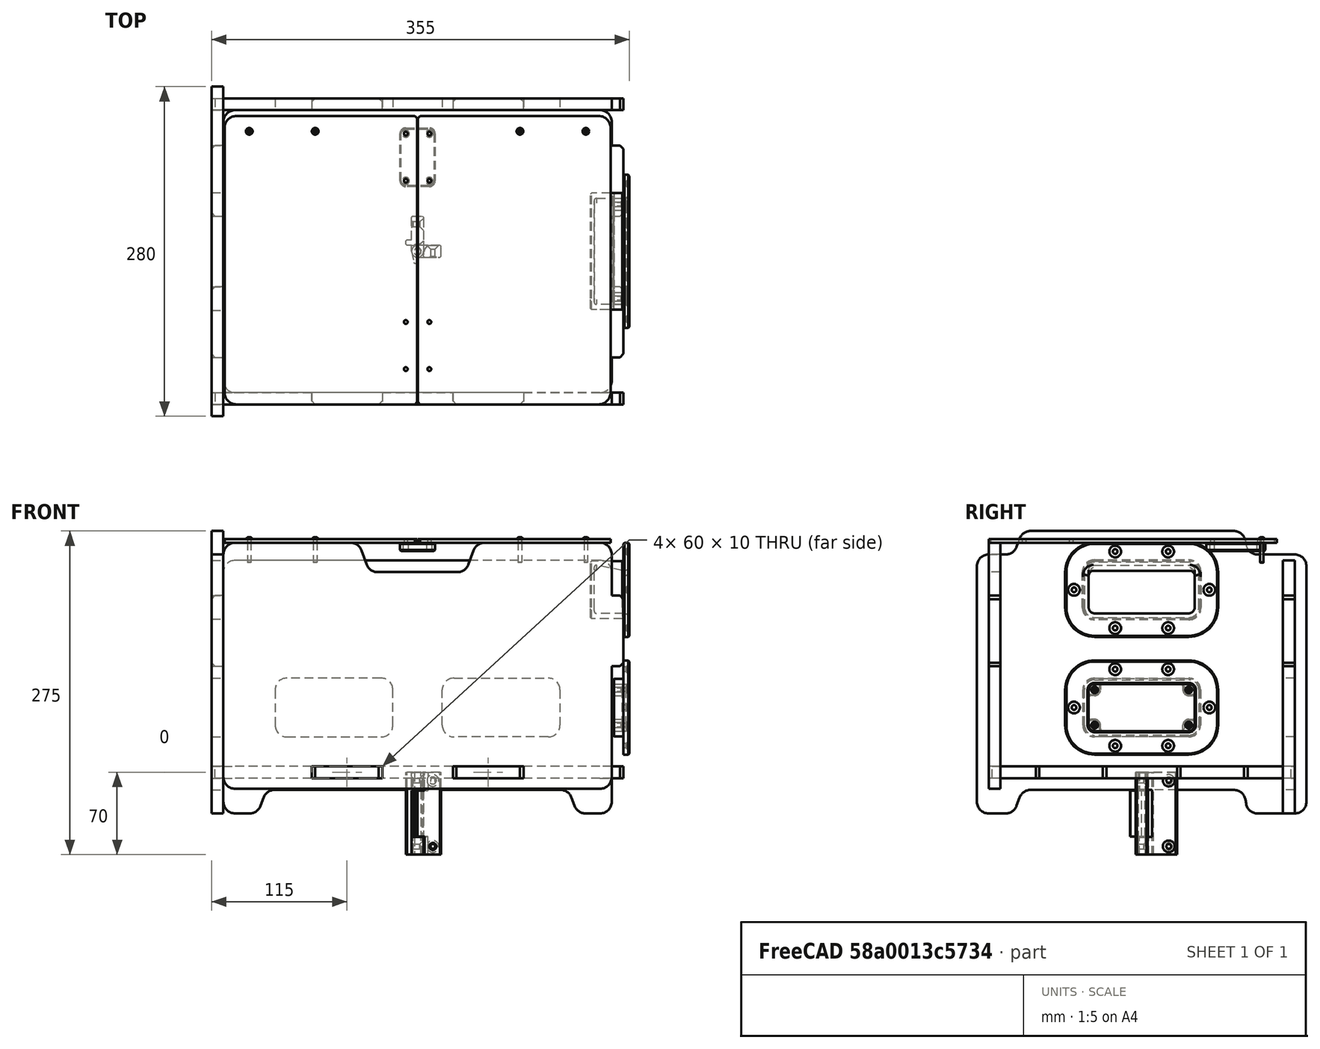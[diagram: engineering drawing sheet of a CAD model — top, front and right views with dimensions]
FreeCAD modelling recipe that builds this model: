
FCSTD DOCUMENT  (FreeCAD 2024.113R14555 (Git shallow))
Label: ModularCrate
License: Creative Commons Attribution-NoDerivatives
LicenseURL: http://creativecommons.org/licenses/by-nd/4.0/
objects: Sketcher::SketchObject×37, PartDesign::Pocket×22, PartDesign::Chamfer×19, PartDesign::Pad×16, PartDesign::Fillet×13, PartDesign::Body×12, App::Link×8, Part::FeaturePython×8, Part::SubShapeBinder×7, TechDraw::DrawSVGTemplate×7, TechDraw::DrawProjGroupItem×7, TechDraw::DrawProjGroup×7, TechDraw::DrawPage×7, App::DocumentObjectGroup×7, PartDesign::Mirrored×6, PartDesign::Plane×5, App::Part×3, PartDesign::FeatureBase×3, PartDesign::SubShapeBinder×2, TechDraw::DrawViewDimension×2, +2 more types
note: 348 computed .brp shape members not serialized (recipe doc carries the construction recipe); baked Part::Feature solids carry a one-line shape summary decoded from their .brp

FEATURE [Sketcher::SketchObject] Sketch007
  ArcFitTolerance = 1e-06
  AttachmentSupport = -> [XY_Plane003]
  ExternalBSplineMaxDegree = 5
  ExternalBSplineTolerance = 0.0001
  FullyConstrained = true
  InternalTolerance = 1e-06
  InvalidShape = false
  MakeInternals = true
  MapMode = 5
  Support = -> [XY_Plane003]
  TreeRank = 69
  ValidateShape = true
  sketch-geometry (10):
    g0: Circle CenterX=-9.7632e-12 CenterY=-2.88622e-11 CenterZ=0 NormalX=0 NormalY=0 NormalZ=1 AngleXU=0 Radius=2.75
    g1: ArcOfCircle CenterX=-9.7632e-12 CenterY=-2.88622e-11 CenterZ=0 NormalX=0 NormalY=0 NormalZ=1 AngleXU=0 Radius=5 StartAngle=3.14159 EndAngle=6.28319
    g2: LineSegment StartX=-5 StartY=-3.9183e-11 StartZ=0 EndX=-5 EndY=5 EndZ=0
    g3: LineSegment StartX=-5 StartY=5 StartZ=0 EndX=-10 EndY=5 EndZ=0
    g4: LineSegment StartX=-10 StartY=5 StartZ=0 EndX=-10 EndY=10 EndZ=0
    g5: LineSegment StartX=-10 StartY=10 StartZ=0 EndX=-5 EndY=10 EndZ=0
    g6: LineSegment StartX=-5 StartY=10 StartZ=0 EndX=-5 EndY=30 EndZ=0
    g7: LineSegment StartX=-5 StartY=30 StartZ=0 EndX=5 EndY=30 EndZ=0
    g8: LineSegment StartX=5 StartY=30 StartZ=0 EndX=5 EndY=7.47242e-11 EndZ=0
    g9: Circle [constr] CenterX=-9.7632e-12 CenterY=-2.88622e-11 CenterZ=0 NormalX=0 NormalY=0 NormalZ=1 AngleXU=0 Radius=5
  constraints (28):
    c: Coincident(g0,g-1)
    c: Coincident(g1,g0)
    c: PointOnObject(g1,g-1)
    c: PointOnObject(g2,g-1)
    c: Vertical(g2)
    c: Coincident(g1,g2)
    c: Coincident(g3,g2)
    c: Horizontal(g3)
    c: Coincident(g4,g3)
    c: Coincident(g5,g4)
    c: Horizontal(g5)
    c: Vertical(g4)
    c: DistanceY(g4,g4) = 5
    c: Diameter(g0) = 5.5
    c: Diameter(g1) = 10
    c: DistanceX(g5,g5) = 5
    c: Vertical(g6)
    c: Coincident(g7,g6)
    c: Horizontal(g7)
    c: Coincident(g8,g1)
    c: Vertical(g8)
    c: Coincident(g8,g7)
    c: Coincident(g5,g6)
    c: PointOnObject(g2,g6)
    c: DistanceY(g6,g6) = 20
    c: Coincident(g9,g0)
    c: PointOnObject(g1,g9)
    c: Tangent(g3,g9)
FEATURE [PartDesign::Pad] Pad004
  AddSubType = 0
  AlongSketchNormal = false
  AutoTaperInnerAngle = true
  CheckUpToFaceLimits = true
  ClaimChildren = false
  Direction = (0,0,1)
  Fit = 0
  FitJoin = 0
  InnerFit = 0
  InnerFitJoin = 0
  InvalidShape = false
  Length = 70
  Length2 = 100
  Linearize = true
  Midplane = true
  NewSolid = false
  Profile = -> Sketch007
  Refine = true
  Suppress = false
  TaperInnerAngle = 0
  TaperInnerAngleRev = 0
  TreeRank = 70
  Type = 0
  ValidateShape = true
  _ProfileBasedVersion = 1
FEATURE [Sketcher::SketchObject] Sketch008
  ArcFitTolerance = 1e-06
  AttachmentSupport = -> [XY_Plane003]
  ExternalBSplineMaxDegree = 5
  ExternalBSplineTolerance = 0.0001
  FullyConstrained = true
  InternalTolerance = 1e-06
  InvalidShape = false
  MakeInternals = true
  MapMode = 5
  Support = -> [XY_Plane003]
  TreeRank = 71
  ValidateShape = true
  sketch-geometry (5):
    g0: LineSegment StartX=-5 StartY=-5 StartZ=0 EndX=-5 EndY=5 EndZ=0
    g1: LineSegment StartX=-5 StartY=5 StartZ=0 EndX=5 EndY=5 EndZ=0
    g2: LineSegment StartX=5 StartY=5 StartZ=0 EndX=5 EndY=-5 EndZ=0
    g3: LineSegment StartX=5 StartY=-5 StartZ=0 EndX=-5 EndY=-5 EndZ=0
    g4: GeomPoint [constr] X=0 Y=0 Z=0
  constraints (12):
    c: Coincident(g0,g1)
    c: Coincident(g1,g2)
    c: Coincident(g2,g3)
    c: Coincident(g3,g0)
    c: Horizontal(g1)
    c: Horizontal(g3)
    c: Vertical(g0)
    c: Vertical(g2)
    c: Symmetric(g1,g0,g4)
    c: Coincident(g4,g-1)
    c: DistanceY(g2,g2) = 10
    c: Equal(g3,g2)
FEATURE [PartDesign::Pocket] Pocket003
  AddSubType = 1
  AutoTaperInnerAngle = true
  BaseFeature = -> Pad004
  CheckUpToFaceLimits = true
  ClaimChildren = false
  Direction = (1,1,1)
  Fit = 0
  FitJoin = 0
  InnerFit = 0
  InnerFitJoin = 0
  InvalidShape = false
  Length = 40
  Length2 = 100
  Linearize = true
  Midplane = true
  NewSolid = false
  Profile = -> Sketch008
  Refine = true
  Suppress = false
  TaperInnerAngle = 0
  TaperInnerAngleRev = 0
  TreeRank = 72
  Type = 0
  ValidateShape = true
  _ProfileBasedVersion = 1
  _Version = 1
FEATURE [Sketcher::SketchObject] Sketch009
  ArcFitTolerance = 1e-06
  AttachmentSupport = -> [XY_Plane003]
  ExternalBSplineMaxDegree = 5
  ExternalBSplineTolerance = 0.0001
  FullyConstrained = true
  InternalTolerance = 1e-06
  InvalidShape = false
  MakeInternals = true
  MapMode = 5
  Support = -> [XY_Plane003]
  TreeRank = 73
  ValidateShape = true
  sketch-geometry (1):
    g0: Circle CenterX=0 CenterY=0 CenterZ=0 NormalX=0 NormalY=0 NormalZ=1 AngleXU=0 Radius=6
  constraints (2):
    c: Coincident(g0,g-1)
    c: Diameter(g0) = 12
FEATURE [PartDesign::Pocket] Pocket004
  AddSubType = 1
  AutoTaperInnerAngle = true
  BaseFeature = -> Pocket003
  CheckUpToFaceLimits = true
  ClaimChildren = false
  Direction = (1,1,1)
  Fit = 0
  FitJoin = 0
  InnerFit = 0
  InnerFitJoin = 0
  InvalidShape = false
  Length = 40
  Length2 = 100
  Linearize = true
  Midplane = true
  NewSolid = false
  Profile = -> Sketch009
  Refine = true
  Suppress = false
  TaperInnerAngle = 0
  TaperInnerAngleRev = 0
  TreeRank = 74
  Type = 0
  ValidateShape = true
  _ProfileBasedVersion = 1
  _Version = 1
FEATURE [PartDesign::Chamfer] Chamfer007
  AddSubType = 0
  Angle = 45
  Base = -> Pocket004 [Edge33]
  BaseFeature = -> Pocket004
  ChamferType = 0
  FlipDirection = false
  InvalidShape = false
  NewSolid = false
  Refine = true
  Size = 0.4
  Size2 = 1
  SupportTransform = false
  Suppress = false
  TreeRank = 75
  UseAllEdges = false
  ValidateShape = true
FEATURE [PartDesign::Chamfer] Chamfer008
  AddSubType = 0
  Angle = 45
  Base = -> Chamfer007 [Edge16,Edge27,Edge44,Edge34]
  BaseFeature = -> Chamfer007
  ChamferType = 0
  FlipDirection = false
  InvalidShape = false
  NewSolid = false
  Refine = true
  Size = 0.4
  Size2 = 1
  SupportTransform = false
  Suppress = false
  TreeRank = 76
  UseAllEdges = false
  ValidateShape = true
FEATURE [PartDesign::Chamfer] Chamfer009
  AddSubType = 0
  Angle = 45
  Base = -> Chamfer008 [Edge17,Edge47,Edge33,Edge54]
  BaseFeature = -> Chamfer008
  ChamferType = 0
  FlipDirection = false
  InvalidShape = false
  NewSolid = false
  Refine = true
  Size = 1
  Size2 = 1
  SupportTransform = false
  Suppress = false
  TreeRank = 77
  UseAllEdges = false
  ValidateShape = true
FEATURE [Sketcher::SketchObject] Sketch010
  ArcFitTolerance = 1e-06
  AttachmentSupport = -> [XY_Plane004]
  ExternalBSplineMaxDegree = 5
  ExternalBSplineTolerance = 0.0001
  FullyConstrained = true
  InternalTolerance = 1e-06
  InvalidShape = false
  MakeInternals = true
  MapMode = 5
  Support = -> [XY_Plane004]
  TreeRank = 88
  ValidateShape = true
  sketch-geometry (8):
    g0: Circle CenterX=-1.7078e-12 CenterY=-5.9561e-12 CenterZ=0 NormalX=0 NormalY=0 NormalZ=1 AngleXU=0 Radius=2.75
    g1: ArcOfCircle CenterX=-1.7078e-12 CenterY=-5.9561e-12 CenterZ=0 NormalX=0 NormalY=0 NormalZ=1 AngleXU=0 Radius=5 StartAngle=8.015e-13 EndAngle=1.5708
    g2: LineSegment StartX=-8.718e-13 StartY=5 StartZ=0 EndX=-10 EndY=3 EndZ=0
    g3: LineSegment StartX=-10 StartY=3 StartZ=0 EndX=-10 EndY=0 EndZ=0
    g4: LineSegment StartX=-10 StartY=0 StartZ=0 EndX=-5 EndY=-1.52707e-11 EndZ=0
    g5: LineSegment StartX=-5 StartY=-1.52707e-11 StartZ=0 EndX=-5 EndY=-20 EndZ=0
    g6: LineSegment StartX=-5 StartY=-20 StartZ=0 EndX=5 EndY=-20 EndZ=0
    g7: LineSegment StartX=5 StartY=-20 StartZ=0 EndX=5 EndY=-7.851e-13 EndZ=0
  constraints (22):
    c: Coincident(g0,g-1)
    c: Diameter(g0) = 5.5
    c: Coincident(g1,g0)
    c: PointOnObject(g1,g-2)
    c: PointOnObject(g1,g-1)
    c: Diameter(g1) = 10
    c: Coincident(g2,g1)
    c: Coincident(g3,g2)
    c: PointOnObject(g3,g-1)
    c: Vertical(g3)
    c: Coincident(g4,g3)
    c: Coincident(g5,g4)
    c: Vertical(g5)
    c: Coincident(g6,g5)
    c: Horizontal(g6)
    c: Coincident(g7,g1)
    c: Vertical(g7)
    c: Coincident(g6,g7)
    c: Symmetric(g4,g1,g0)
    c: DistanceX(g4,g4) = 5
    c: DistanceY(g3,g3) = 3
    c: DistanceY(g5,g5) = 20
FEATURE [PartDesign::Pad] Pad005
  AddSubType = 0
  AlongSketchNormal = false
  AutoTaperInnerAngle = true
  CheckUpToFaceLimits = true
  ClaimChildren = false
  Direction = (0,0,1)
  Fit = 0
  FitJoin = 0
  InnerFit = 0
  InnerFitJoin = 0
  InvalidShape = false
  Length = 70
  Length2 = 100
  Linearize = true
  Midplane = true
  NewSolid = false
  Profile = -> Sketch010
  Refine = true
  Suppress = false
  TaperInnerAngle = 0
  TaperInnerAngleRev = 0
  TreeRank = 89
  Type = 0
  ValidateShape = true
  _ProfileBasedVersion = 1
FEATURE [Sketcher::SketchObject] Sketch011
  ArcFitTolerance = 1e-06
  AttachmentOffset = pos=(0,0,19.5) rot=(0,0,1;0rad)
  AttachmentSupport = -> [XY_Plane004]
  ExternalBSplineMaxDegree = 5
  ExternalBSplineTolerance = 0.0001
  FullyConstrained = true
  InternalTolerance = 1e-06
  InvalidShape = false
  MakeInternals = true
  MapMode = 5
  Placement = pos=(0,0,19.5) rot=(0,0,1;0rad)
  Support = -> [XY_Plane004]
  TreeRank = 90
  ValidateShape = true
  sketch-geometry (5):
    g0: LineSegment StartX=-15 StartY=5 StartZ=0 EndX=-15 EndY=-5 EndZ=0
    g1: LineSegment StartX=-15 StartY=-5 StartZ=0 EndX=5 EndY=-5 EndZ=0
    g2: LineSegment StartX=5 StartY=-5 StartZ=0 EndX=5 EndY=5 EndZ=0
    g3: LineSegment StartX=5 StartY=5 StartZ=0 EndX=-15 EndY=5 EndZ=0
    g4: GeomPoint [constr] X=-5 Y=1.1738e-12 Z=0
  constraints (13):
    c: Coincident(g0,g1)
    c: Coincident(g1,g2)
    c: Coincident(g2,g3)
    c: Coincident(g3,g0)
    c: Horizontal(g1)
    c: Horizontal(g3)
    c: Vertical(g0)
    c: Vertical(g2)
    c: Symmetric(g1,g0,g4)
    c: PointOnObject(g4,g-1)
    c: DistanceY(g2,g2) = 10
    c: DistanceX(g-1,g2) = 5
    c: DistanceX(g3,g3) = 20
FEATURE [PartDesign::Pocket] Pocket005
  AddSubType = 1
  AutoTaperInnerAngle = true
  BaseFeature = -> Pad005
  CheckUpToFaceLimits = true
  ClaimChildren = false
  Direction = (1,1,1)
  Fit = 0
  FitJoin = 0
  InnerFit = 0
  InnerFitJoin = 0
  InvalidShape = false
  Length = 5
  Length2 = 100
  Linearize = true
  NewSolid = false
  Profile = -> Sketch011
  Refine = true
  Reversed = true
  Suppress = false
  TaperInnerAngle = 0
  TaperInnerAngleRev = 0
  TreeRank = 91
  Type = 1
  ValidateShape = true
  _ProfileBasedVersion = 1
  _Version = 1
FEATURE [PartDesign::Mirrored] Mirrored
  AddSubType = 0
  BaseFeature = -> Pocket005
  CopyShape = false
  InvalidShape = false
  MirrorPlane = -> XY_Plane004
  NewSolid = false
  OriginalSubs = -> [Pocket005]
  Originals = -> [Pocket005]
  ParallelTransform = true
  Refine = true
  SubTransform = true
  Suppress = false
  TreeRank = 92
  ValidateShape = true
  _Version = 3
FEATURE [PartDesign::Chamfer] Chamfer010
  AddSubType = 0
  Angle = 45
  Base = -> Mirrored [Edge12,Edge32]
  BaseFeature = -> Mirrored
  ChamferType = 0
  FlipDirection = false
  InvalidShape = false
  NewSolid = false
  Refine = true
  Size = 0.4
  Size2 = 1
  SupportTransform = false
  Suppress = false
  TreeRank = 93
  UseAllEdges = false
  ValidateShape = true
FEATURE [Sketcher::SketchObject] Sketch012
  ArcFitTolerance = 1e-06
  AttachmentSupport = -> [Chamfer010]
  ExternalBSplineMaxDegree = 5
  ExternalBSplineTolerance = 0.0001
  FullyConstrained = true
  InternalTolerance = 1e-06
  InvalidShape = false
  MakeInternals = true
  MapMode = 5
  Placement = pos=(0,0,19.5) rot=(0,0,1;0rad)
  Support = -> [Chamfer010]
  TreeRank = 94
  ValidateShape = true
  sketch-geometry (1):
    g0: Circle CenterX=0 CenterY=0 CenterZ=0 NormalX=0 NormalY=0 NormalZ=1 AngleXU=0 Radius=5.5
  constraints (2):
    c: Coincident(g0,g-1)
    c: Diameter(g0) = 11
FEATURE [PartDesign::Pocket] Pocket006
  AddSubType = 1
  AutoTaperInnerAngle = true
  BaseFeature = -> Chamfer010
  CheckUpToFaceLimits = true
  ClaimChildren = false
  Direction = (1,1,1)
  Fit = 0
  FitJoin = 0
  InnerFit = 0
  InnerFitJoin = 0
  InvalidShape = false
  Length = 5
  Length2 = 100
  Linearize = true
  NewSolid = false
  Profile = -> Sketch012
  Refine = true
  Reversed = true
  Suppress = false
  TaperInnerAngle = 0
  TaperInnerAngleRev = 0
  TreeRank = 95
  Type = 1
  ValidateShape = true
  _ProfileBasedVersion = 1
  _Version = 1
FEATURE [PartDesign::Mirrored] Mirrored001
  AddSubType = 0
  BaseFeature = -> Pocket006
  CopyShape = false
  InvalidShape = false
  MirrorPlane = -> XY_Plane004
  NewSolid = false
  OriginalSubs = -> [Pocket006]
  Originals = -> [Pocket006]
  ParallelTransform = true
  Refine = true
  SubTransform = true
  Suppress = false
  TreeRank = 96
  ValidateShape = true
  _Version = 3
FEATURE [PartDesign::Chamfer] Chamfer011
  AddSubType = 0
  Angle = 45
  Base = -> Mirrored001 [Edge52,Edge50,Edge42,Edge40]
  BaseFeature = -> Mirrored001
  ChamferType = 0
  FlipDirection = false
  InvalidShape = false
  NewSolid = false
  Refine = true
  Size = 0.4
  Size2 = 1
  SupportTransform = false
  Suppress = false
  TreeRank = 97
  UseAllEdges = false
  ValidateShape = true
FEATURE [PartDesign::Chamfer] Chamfer012
  AddSubType = 0
  Angle = 45
  Base = -> Chamfer011 [Edge16,Edge34,Edge39,Edge25,Edge21,Edge43]
  BaseFeature = -> Chamfer011
  ChamferType = 0
  FlipDirection = false
  InvalidShape = false
  NewSolid = false
  Refine = true
  Size = 1
  Size2 = 1
  SupportTransform = false
  Suppress = false
  TreeRank = 98
  UseAllEdges = false
  ValidateShape = true
FEATURE [Sketcher::SketchObject] Sketch013
  ArcFitTolerance = 1e-06
  AttachmentSupport = -> [YZ_Plane004]
  ExternalBSplineMaxDegree = 5
  ExternalBSplineTolerance = 0.0001
  ExternalGeometry = -> [Chamfer012]
  FullyConstrained = true
  InternalTolerance = 1e-06
  InvalidShape = false
  MakeInternals = true
  MapMode = 5
  Placement = pos=(0,0,0) rot=(0.57735,0.57735,0.57735;2.0944rad)
  Support = -> [YZ_Plane004]
  TreeRank = 99
  ValidateShape = true
  sketch-geometry (2):
    g0: Circle CenterX=-13 CenterY=28 CenterZ=0 NormalX=0 NormalY=0 NormalZ=1 AngleXU=0 Radius=2
    g1: Circle CenterX=-13 CenterY=-28 CenterZ=0 NormalX=0 NormalY=0 NormalZ=1 AngleXU=0 Radius=2
  constraints (5):
    c: Diameter(g0) = 4
    c: DistanceX(g-3,g0) = 7
    c: DistanceY(g0,g-3) = 7
    c: Equal(g1,g0)
    c: Symmetric(g1,g0,g-1)
FEATURE [PartDesign::Pocket] Pocket007
  AddSubType = 1
  AutoTaperInnerAngle = true
  BaseFeature = -> Chamfer012
  CheckUpToFaceLimits = true
  ClaimChildren = false
  Direction = (1,1,1)
  Fit = 0
  FitJoin = 0
  InnerFit = 0
  InnerFitJoin = 0
  InvalidShape = false
  Length = 5
  Length2 = 100
  Linearize = true
  Midplane = true
  NewSolid = false
  Profile = -> Sketch013
  Refine = true
  Suppress = false
  TaperInnerAngle = 0
  TaperInnerAngleRev = 0
  TreeRank = 100
  Type = 1
  ValidateShape = true
  _ProfileBasedVersion = 1
  _Version = 1
FEATURE [PartDesign::Chamfer] Chamfer013
  AddSubType = 0
  Angle = 45
  Base = -> Pocket007 [Edge34,Edge33]
  BaseFeature = -> Pocket007
  ChamferType = 0
  FlipDirection = false
  InvalidShape = false
  NewSolid = false
  Refine = true
  Size = 1
  Size2 = 1
  SupportTransform = false
  Suppress = false
  TreeRank = 101
  UseAllEdges = false
  ValidateShape = true
FEATURE [Sketcher::SketchObject] Sketch014
  ArcFitTolerance = 1e-06
  AttachmentSupport = -> [YZ_Plane003]
  ExternalBSplineMaxDegree = 5
  ExternalBSplineTolerance = 0.0001
  ExternalGeometry = -> [Chamfer009]
  FullyConstrained = true
  InternalTolerance = 1e-06
  InvalidShape = false
  MakeInternals = true
  MapMode = 5
  Placement = pos=(0,0,0) rot=(0.57735,0.57735,0.57735;2.0944rad)
  Support = -> [YZ_Plane003]
  TreeRank = 102
  ValidateShape = true
  sketch-geometry (2):
    g0: Circle CenterX=23 CenterY=28 CenterZ=0 NormalX=0 NormalY=0 NormalZ=1 AngleXU=0 Radius=2
    g1: Circle CenterX=23 CenterY=-28 CenterZ=0 NormalX=0 NormalY=0 NormalZ=1 AngleXU=0 Radius=2
  constraints (5):
    c: DistanceX(g0,g-3) = 7
    c: DistanceY(g0,g-3) = 7
    c: Symmetric(g1,g0,g-1)
    c: Equal(g1,g0)
    c: Diameter(g1) = 4
FEATURE [PartDesign::Pocket] Pocket008
  AddSubType = 1
  AutoTaperInnerAngle = true
  BaseFeature = -> Chamfer009
  CheckUpToFaceLimits = true
  ClaimChildren = false
  Direction = (1,1,1)
  Fit = 0
  FitJoin = 0
  InnerFit = 0
  InnerFitJoin = 0
  InvalidShape = false
  Length = 5
  Length2 = 100
  Linearize = true
  Midplane = true
  NewSolid = false
  Profile = -> Sketch014
  Refine = true
  Suppress = false
  TaperInnerAngle = 0
  TaperInnerAngleRev = 0
  TreeRank = 103
  Type = 1
  ValidateShape = true
  _ProfileBasedVersion = 1
  _Version = 1
FEATURE [PartDesign::Chamfer] Chamfer014
  AddSubType = 0
  Angle = 45
  Base = -> Pocket008 [Edge64,Edge63]
  BaseFeature = -> Pocket008
  ChamferType = 0
  FlipDirection = false
  InvalidShape = false
  NewSolid = false
  Refine = true
  Size = 1
  Size2 = 1
  SupportTransform = false
  Suppress = false
  TreeRank = 104
  UseAllEdges = false
  ValidateShape = true
FEATURE [PartDesign::Chamfer] Chamfer019
  AddSubType = 0
  Angle = 45
  Base = -> Chamfer014 [Edge45,Edge38]
  BaseFeature = -> Chamfer014
  ChamferType = 0
  FlipDirection = false
  InvalidShape = false
  NewSolid = false
  Refine = true
  Size = 3
  Size2 = 1
  SupportTransform = false
  Suppress = false
  TreeRank = 128
  UseAllEdges = false
  ValidateShape = true
FEATURE [PartDesign::Chamfer] Chamfer020
  AddSubType = 0
  Angle = 45
  Base = -> Chamfer013 [Edge76,Edge87]
  BaseFeature = -> Chamfer013
  ChamferType = 0
  FlipDirection = false
  InvalidShape = false
  NewSolid = false
  Refine = true
  Size = 3
  Size2 = 1
  SupportTransform = false
  Suppress = false
  TreeRank = 129
  UseAllEdges = false
  ValidateShape = true
FEATURE [Sketcher::SketchObject] Sketch017
  ArcFitTolerance = 1e-06
  AttachmentSupport = -> [Chamfer020]
  ExternalBSplineMaxDegree = 5
  ExternalBSplineTolerance = 0.0001
  ExternalGeometry = -> [Chamfer020]
  FullyConstrained = true
  InternalTolerance = 1e-06
  InvalidShape = false
  MakeInternals = true
  MapMode = 5
  Placement = pos=(0,0,35) rot=(0,0,1;0rad)
  Support = -> [Chamfer020]
  TreeRank = 130
  ValidateShape = true
  sketch-geometry (3):
    g0: LineSegment StartX=5 StartY=-5 StartZ=0 EndX=1 EndY=-5 EndZ=0
    g1: LineSegment StartX=1 StartY=-5 StartZ=0 EndX=5 EndY=-9 EndZ=0
    g2: LineSegment StartX=5 StartY=-9 StartZ=0 EndX=5 EndY=-5 EndZ=0
  constraints (8):
    c: Coincident(g0,g-3)
    c: Horizontal(g0)
    c: Coincident(g2,g1)
    c: Coincident(g2,g0)
    c: Coincident(g0,g1)
    c: Vertical(g2)
    c: Equal(g2,g0)
    c: DistanceY(g2,g2) = 4
FEATURE [PartDesign::Pocket] Pocket010
  AddSubType = 1
  AutoTaperInnerAngle = true
  BaseFeature = -> Chamfer020
  CheckUpToFaceLimits = true
  ClaimChildren = false
  Direction = (1,1,1)
  Fit = 0
  FitJoin = 0
  InnerFit = 0
  InnerFitJoin = 0
  InvalidShape = false
  Length = 15.5
  Length2 = 100
  Linearize = true
  NewSolid = false
  Profile = -> Sketch017
  Refine = true
  Suppress = false
  TaperInnerAngle = 0
  TaperInnerAngleRev = 0
  TreeRank = 131
  Type = 0
  ValidateShape = true
  _ProfileBasedVersion = 1
  _Version = 1
FEATURE [PartDesign::Mirrored] Mirrored002
  AddSubType = 0
  BaseFeature = -> Pocket010
  CopyShape = false
  InvalidShape = false
  MirrorPlane = -> XY_Plane004
  NewSolid = false
  OriginalSubs = -> [Pocket010]
  Originals = -> [Pocket010]
  ParallelTransform = true
  Refine = true
  SubTransform = true
  Suppress = false
  TreeRank = 132
  ValidateShape = true
  _Version = 3
FEATURE [Sketcher::SketchObject] Sketch018
  ArcFitTolerance = 1e-06
  AttachmentSupport = -> [XY_Plane003]
  ExternalBSplineMaxDegree = 5
  ExternalBSplineTolerance = 0.0001
  ExternalGeometry = -> [Chamfer019]
  FullyConstrained = true
  InternalTolerance = 1e-06
  InvalidShape = false
  MakeInternals = true
  MapMode = 5
  Support = -> [XY_Plane003]
  TreeRank = 133
  ValidateShape = true
  sketch-geometry (3):
    g0: LineSegment StartX=5 StartY=9 StartZ=0 EndX=1 EndY=5 EndZ=0
    g1: LineSegment StartX=1 StartY=5 StartZ=0 EndX=5 EndY=5 EndZ=0
    g2: LineSegment StartX=5 StartY=9 StartZ=0 EndX=5 EndY=5 EndZ=0
  constraints (8):
    c: PointOnObject(g0,g-3)
    c: Coincident(g1,g0)
    c: Coincident(g1,g-4)
    c: Horizontal(g1)
    c: Coincident(g2,g0)
    c: Coincident(g2,g1)
    c: Equal(g2,g1)
    c: DistanceY(g2,g2) = 4
FEATURE [PartDesign::Pocket] Pocket011
  AddSubType = 1
  AutoTaperInnerAngle = true
  BaseFeature = -> Chamfer019
  CheckUpToFaceLimits = true
  ClaimChildren = false
  Direction = (1,1,1)
  Fit = 0
  FitJoin = 0
  InnerFit = 0
  InnerFitJoin = 0
  InvalidShape = false
  Length = 40
  Length2 = 100
  Linearize = true
  Midplane = true
  NewSolid = false
  Profile = -> Sketch018
  Refine = true
  Suppress = false
  TaperInnerAngle = 0
  TaperInnerAngleRev = 0
  TreeRank = 134
  Type = 0
  ValidateShape = true
  _ProfileBasedVersion = 1
  _Version = 1
FEATURE [PartDesign::Fillet] Fillet006
  AddSubType = 0
  Base = -> Mirrored002 [Edge59,Edge14]
  BaseFeature = -> Mirrored002
  InvalidShape = false
  NewSolid = false
  Radius = 5
  Refine = true
  SupportTransform = false
  Suppress = false
  TreeRank = 135
  UseAllEdges = false
  ValidateShape = true
FEATURE [PartDesign::Body] Body004  label="HingePart02"
  AutoGroupSolids = false
  ClaimAllChildren = false
  ExportMode = 0
  Group = -> [Sketch010,Pad005,Sketch011,Pocket005,Mirrored,Chamfer010,Sketch012,Pocket006,Mirrored001,Chamfer011,Chamfer012,Sketch013,Pocket007,Chamfer013,Chamfer020,Sketch017,Pocket010,Mirrored002,Fillet006]
  InvalidShape = false
  Origin = -> Origin005
  Placement = pos=(0,0,0) rot=(0,0,1;1.5708rad)
  SingleSolid = true
  Tip = -> Fillet006
  TreeRank = 87
  ValidateShape = true
  _ExportChildren = -> [Pad005,Pocket005,Mirrored,Chamfer010,Pocket006,Mirrored001,Chamfer011,Chamfer012,Pocket007,Chamfer013,Chamfer020,Pocket010,Mirrored002,Fillet006]
  _GroupVersion = 1
FEATURE [PartDesign::Fillet] Fillet007
  AddSubType = 0
  Base = -> Pocket011 [Edge44]
  BaseFeature = -> Pocket011
  InvalidShape = false
  NewSolid = false
  Radius = 5
  Refine = true
  SupportTransform = false
  Suppress = false
  TreeRank = 136
  UseAllEdges = false
  ValidateShape = true
FEATURE [PartDesign::Body] Body003  label="HingePart01"
  AutoGroupSolids = false
  ClaimAllChildren = false
  ExportMode = 0
  Group = -> [Sketch007,Pad004,Sketch008,Pocket003,Sketch009,Pocket004,Chamfer007,Chamfer008,Chamfer009,Sketch014,Pocket008,Chamfer014,Chamfer019,Sketch018,Pocket011,Fillet007]
  InvalidShape = false
  Origin = -> Origin004
  SingleSolid = true
  Tip = -> Fillet007
  TreeRank = 68
  ValidateShape = true
  _ExportChildren = -> [Pad004,Pocket003,Pocket004,Chamfer007,Chamfer008,Chamfer009,Pocket008,Chamfer014,Chamfer019,Pocket011,Fillet007]
  _GroupVersion = 1
FEATURE [App::Part] Part  label="Hinge"
  ClaimAllChildren = false
  ExportMode = 1
  Group = -> [Body003,Body004]
  Origin = -> Origin003
  Placement = pos=(-115,115,225) rot=(0.57735,-0.57735,0.57735;4.18879rad)
  TreeRank = 58
  _ExportChildren = -> [Body003,Body004]
  _GroupVersion = 1
FEATURE [PartDesign::Plane] DatumPlane  label="Back"
  AttachmentOffset = pos=(0,0,30) rot=(0,0,1;0rad)
  AttachmentSupport = -> [XY_Plane007]
  InvalidShape = false
  Length = 10
  MapMode = 5
  MinimumLength = 10
  MinimumWidth = 10
  Placement = pos=(0,0,30) rot=(0,0,1;0rad)
  ResizeMode = 0
  Support = -> [XY_Plane007]
  TreeRank = 171
  ValidateShape = true
  Width = 10
FEATURE [PartDesign::Plane] DatumPlane001  label="Front"
  AttachmentOffset = pos=(0,0,130) rot=(0,0,1;0rad)
  AttachmentSupport = -> [XZ_Plane007]
  InvalidShape = false
  Length = 10
  MapMode = 5
  MinimumLength = 10
  MinimumWidth = 10
  Placement = pos=(0,-130,2.89e-14) rot=(1,0,0;1.5708rad)
  ResizeMode = 0
  Support = -> [XZ_Plane007]
  TreeRank = 184
  ValidateShape = true
  Width = 10
FEATURE [PartDesign::Plane] DatumPlane002  label="Rear"
  AttachmentOffset = pos=(0,0,-130) rot=(0,0,1;0rad)
  AttachmentSupport = -> [XZ_Plane007]
  InvalidShape = false
  Length = 10
  MapMode = 5
  MinimumLength = 10
  MinimumWidth = 10
  Placement = pos=(0,130,-2.89e-14) rot=(1,0,0;1.5708rad)
  ResizeMode = 0
  Support = -> [XZ_Plane007]
  TreeRank = 185
  ValidateShape = true
  Width = 10
FEATURE [PartDesign::Plane] DatumPlane003  label="Right"
  AttachmentOffset = pos=(0,0,165) rot=(0,0,1;0rad)
  AttachmentSupport = -> [YZ_Plane007]
  InvalidShape = false
  Length = 10
  MapMode = 5
  MinimumLength = 10
  MinimumWidth = 10
  Placement = pos=(165,-3.66e-14,3.66e-14) rot=(0.57735,0.57735,0.57735;2.0944rad)
  ResizeMode = 0
  Support = -> [YZ_Plane007]
  TreeRank = 186
  ValidateShape = true
  Width = 10
FEATURE [PartDesign::Plane] DatumPlane004  label="Left"
  AttachmentOffset = pos=(0,0,-165) rot=(0,0,1;0rad)
  AttachmentSupport = -> [YZ_Plane007]
  InvalidShape = false
  Length = 546
  MapMode = 5
  MinimumLength = 10
  MinimumWidth = 10
  Placement = pos=(-165,3.66e-14,-3.66e-14) rot=(0.57735,0.57735,0.57735;2.0944rad)
  ResizeMode = 0
  Support = -> [YZ_Plane007]
  TreeRank = 187
  ValidateShape = true
  Width = 726
FEATURE [Part::SubShapeBinder] Import  label="Import(Back)"
  BindCopyOnChange = 0
  BindMode = 0
  ClaimChildren = false
  Context = -> Part001 [Body007.Import.]
  EdgeTolerance = 1e-06
  FillStyle = 0
  Fuse = false
  InvalidShape = false
  MakeFace = false
  MergeEdges = true
  OffsetFill = false
  OffsetIntersection = false
  OffsetJoinType = 0
  OffsetOpenResult = false
  Outline = false
  PartialLoad = false
  Relative = true
  SplitEdges = false
  Support = -> [DatumPlane]
  TightBound = false
  TreeRank = 198
  ValidateShape = true
  _Version = 8
FEATURE [Sketcher::SketchObject] Sketch021
  ArcFitTolerance = 1e-06
  AttachmentSupport = -> [Import]
  ExternalBSplineMaxDegree = 5
  ExternalBSplineTolerance = 0.0001
  FullyConstrained = true
  InternalTolerance = 1e-06
  InvalidShape = false
  MakeInternals = true
  MapMode = 5
  Placement = pos=(0,0,30) rot=(0,0,1;0rad)
  Support = -> [Import]
  TreeRank = 199
  ValidateShape = true
  sketch-geometry (5):
    g0: LineSegment StartX=-165 StartY=120 StartZ=0 EndX=-165 EndY=-120 EndZ=0
    g1: LineSegment StartX=-165 StartY=-120 StartZ=0 EndX=165 EndY=-120 EndZ=0
    g2: LineSegment StartX=165 StartY=-120 StartZ=0 EndX=165 EndY=120 EndZ=0
    g3: LineSegment StartX=165 StartY=120 StartZ=0 EndX=-165 EndY=120 EndZ=0
    g4: GeomPoint [constr] X=0 Y=0 Z=0
  constraints (12):
    c: Coincident(g0,g1)
    c: Coincident(g1,g2)
    c: Coincident(g2,g3)
    c: Coincident(g3,g0)
    c: Horizontal(g1)
    c: Horizontal(g3)
    c: Vertical(g0)
    c: Vertical(g2)
    c: Symmetric(g1,g0,g4)
    c: Coincident(g4,g-1)
    c: DistanceX(g3,g3) = 330
    c: DistanceY(g2,g2) = 240
FEATURE [PartDesign::Pad] Pad008
  AddSubType = 0
  AlongSketchNormal = false
  AutoTaperInnerAngle = true
  CheckUpToFaceLimits = true
  ClaimChildren = false
  Direction = (0,0,1)
  Fit = 0
  FitJoin = 0
  InnerFit = 0
  InnerFitJoin = 0
  InvalidShape = false
  Length = 10
  Length2 = 100
  Linearize = true
  NewSolid = false
  Profile = -> Sketch021
  Refine = true
  Suppress = false
  TaperInnerAngle = 0
  TaperInnerAngleRev = 0
  TreeRank = 200
  Type = 0
  ValidateShape = true
  _ProfileBasedVersion = 1
FEATURE [Part::SubShapeBinder] Import001  label="Import001(Pad008)"
  BindCopyOnChange = 0
  BindMode = 0
  ClaimChildren = false
  Context = -> Part001 [Body008.Import001.]
  EdgeTolerance = 1e-06
  FillStyle = 0
  Fuse = false
  InvalidShape = false
  MakeFace = false
  MergeEdges = true
  OffsetFill = false
  OffsetIntersection = false
  OffsetJoinType = 0
  OffsetOpenResult = false
  Outline = false
  PartialLoad = false
  Relative = true
  SplitEdges = false
  Support = -> [Body007[Pad008.]]
  TightBound = false
  TreeRank = 212
  ValidateShape = true
  _Version = 8
FEATURE [Sketcher::SketchObject] Sketch022
  ArcFitTolerance = 1e-06
  AttachmentSupport = -> [YZ_Plane009]
  ExternalBSplineMaxDegree = 5
  ExternalBSplineTolerance = 0.0001
  ExternalGeometry = -> [Import001]
  FullyConstrained = true
  InternalTolerance = 1e-06
  InvalidShape = false
  MakeInternals = true
  MapMode = 5
  Placement = pos=(0,0,0) rot=(0.57735,0.57735,0.57735;2.0944rad)
  Support = -> [YZ_Plane009]
  TreeRank = 211
  ValidateShape = true
  sketch-geometry (4):
    g0: LineSegment StartX=-140 StartY=240 StartZ=0 EndX=140 EndY=240 EndZ=0
    g1: LineSegment StartX=140 StartY=240 StartZ=0 EndX=140 EndY=0 EndZ=0
    g2: LineSegment StartX=140 StartY=0 StartZ=0 EndX=-140 EndY=0 EndZ=0
    g3: LineSegment StartX=-140 StartY=0 StartZ=0 EndX=-140 EndY=240 EndZ=0
  constraints (12):
    c: Coincident(g0,g1)
    c: Coincident(g1,g2)
    c: Coincident(g2,g3)
    c: Coincident(g3,g0)
    c: Horizontal(g0)
    c: Horizontal(g2)
    c: Vertical(g1)
    c: Vertical(g3)
    c: PointOnObject(g1,g-1)
    c: DistanceX(g0,g0) = 280
    c: DistanceX(g2,g-3) = 20
    c: DistanceY(g1,g1) = 240
FEATURE [PartDesign::Pad] Pad009
  AddSubType = 0
  AlongSketchNormal = false
  AutoTaperInnerAngle = true
  CheckUpToFaceLimits = true
  ClaimChildren = false
  Direction = (1,-2e-16,3e-16)
  Fit = 0
  FitJoin = 0
  InnerFit = 0
  InnerFitJoin = 0
  InvalidShape = false
  Length = 10
  Length2 = 100
  Linearize = true
  NewSolid = false
  Profile = -> Sketch022
  Refine = true
  Suppress = false
  TaperInnerAngle = 0
  TaperInnerAngleRev = 0
  TreeRank = 213
  Type = 0
  ValidateShape = true
  _ProfileBasedVersion = 1
FEATURE [Sketcher::SketchObject] Sketch024
  ArcFitTolerance = 1e-06
  AttachmentSupport = -> [XZ_Plane012]
  ExternalBSplineMaxDegree = 5
  ExternalBSplineTolerance = 0.0001
  FullyConstrained = true
  InternalTolerance = 1e-06
  InvalidShape = false
  MakeInternals = true
  MapMode = 5
  Placement = pos=(0,0,0) rot=(1,0,0;1.5708rad)
  Support = -> [XZ_Plane012]
  TreeRank = 247
  ValidateShape = true
  sketch-geometry (5):
    g0: LineSegment StartX=-165 StartY=215 StartZ=0 EndX=-165 EndY=8.53e-14 EndZ=0
    g1: LineSegment StartX=-165 StartY=9.41e-14 StartZ=0 EndX=165 EndY=9.41e-14 EndZ=0
    g2: LineSegment StartX=165 StartY=9.41e-14 StartZ=0 EndX=165 EndY=215 EndZ=0
    g3: LineSegment StartX=165 StartY=215 StartZ=0 EndX=-165 EndY=215 EndZ=0
    g4: GeomPoint [constr] X=2.79e-14 Y=107.5 Z=0
  constraints (13):
    c: Coincident(g0,g1)
    c: Coincident(g1,g2)
    c: Coincident(g2,g3)
    c: Coincident(g3,g0)
    c: Horizontal(g1)
    c: Horizontal(g3)
    c: Vertical(g0)
    c: Vertical(g2)
    c: Symmetric(g1,g0,g4)
    c: PointOnObject(g4,g-2)
    c: PointOnObject(g1,g-1)
    c: DistanceY(g2,g2) = 215
    c: DistanceX(g3,g3) = 330
FEATURE [PartDesign::Pad] Pad011
  AddSubType = 0
  AlongSketchNormal = false
  AutoTaperInnerAngle = true
  CheckUpToFaceLimits = true
  ClaimChildren = false
  Direction = (0,-1,-2e-16)
  Fit = 0
  FitJoin = 0
  InnerFit = 0
  InnerFitJoin = 0
  InvalidShape = false
  Length = 10
  Length2 = 100
  Linearize = true
  NewSolid = false
  Profile = -> Sketch024
  Refine = true
  Suppress = false
  TaperInnerAngle = 0
  TaperInnerAngleRev = 0
  TreeRank = 248
  Type = 0
  ValidateShape = true
  _ProfileBasedVersion = 1
FEATURE [Sketcher::SketchObject] Sketch025
  ArcFitTolerance = 1e-06
  AttachmentSupport = -> [YZ_Plane009]
  ExternalBSplineMaxDegree = 5
  ExternalBSplineTolerance = 0.0001
  ExternalGeometry = -> [Pad009]
  FullyConstrained = true
  InternalTolerance = 1e-06
  InvalidShape = false
  MakeInternals = true
  MapMode = 5
  Placement = pos=(0,0,0) rot=(0.57735,0.57735,0.57735;2.0944rad)
  Support = -> [YZ_Plane009]
  TreeRank = 249
  ValidateShape = true
  sketch-geometry (14):
    g0: LineSegment StartX=-108.64 StartY=0 StartZ=0 EndX=-101.36 EndY=20 EndZ=0
    g1: LineSegment StartX=-101.36 StartY=20 StartZ=0 EndX=86.6397 EndY=20 EndZ=0
    g2: LineSegment StartX=86.6397 StartY=20 StartZ=0 EndX=90.1662 EndY=0 EndZ=0
    g3: LineSegment StartX=90.1662 StartY=0 StartZ=0 EndX=-108.64 EndY=0 EndZ=0
    g4: LineSegment [constr] StartX=-105 StartY=10 StartZ=0 EndX=-140 EndY=10 EndZ=0
    g5: LineSegment StartX=-140 StartY=220 StartZ=0 EndX=-108.64 EndY=220 EndZ=0
    g6: LineSegment StartX=-108.64 StartY=220 StartZ=0 EndX=-101.36 EndY=240 EndZ=0
    g7: LineSegment StartX=-101.36 StartY=240 StartZ=0 EndX=-140 EndY=240 EndZ=0
    g8: LineSegment StartX=-140 StartY=240 StartZ=0 EndX=-140 EndY=220 EndZ=0
    g9: LineSegment StartX=140 StartY=240 StartZ=0 EndX=86.6397 EndY=240 EndZ=0
    g10: LineSegment StartX=86.6397 StartY=240 StartZ=0 EndX=90.1662 EndY=220 EndZ=0
    g11: LineSegment StartX=90.1662 StartY=220 StartZ=0 EndX=140 EndY=220 EndZ=0
    g12: LineSegment StartX=140 StartY=220 StartZ=0 EndX=140 EndY=240 EndZ=0
    g13: LineSegment [constr] StartX=86.6397 StartY=20 StartZ=0 EndX=86.6397 EndY=0 EndZ=0
  constraints (41):
    c: PointOnObject(g0,g-1)
    c: Coincident(g1,g0)
    c: Horizontal(g1)
    c: Coincident(g2,g1)
    c: PointOnObject(g2,g-1)
    c: Coincident(g3,g0)
    c: Angle(g3,g0) = 1.22173
    c: Coincident(g2,g3)
    c: Angle(g2,g3) = 1.39626
    c: DistanceY(g2,g1) = 20
    c: PointOnObject(g4,g0)
    c: PointOnObject(g4,g-3)
    c: Horizontal(g4)
    c: DistanceY(g-3,g4) = 10
    c: DistanceX(g4,g4) = 35
    c: DistanceX(g1,g1) = 188
    c: PointOnObject(g5,g-3)
    c: Horizontal(g5)
    c: Coincident(g6,g5)
    c: Coincident(g6,g7)
    c: Coincident(g7,g-3)
    c: Horizontal(g7)
    c: Coincident(g7,g8)
    c: Coincident(g8,g5)
    c: Coincident(g-4,g9)
    c: Horizontal(g9)
    c: Coincident(g9,g10)
    c: Coincident(g10,g11)
    c: PointOnObject(g11,g-4)
    c: Coincident(g11,g12)
    c: Coincident(g12,g9)
    c: Horizontal(g11)
    c: Horizontal(g10,g5)
    c: Coincident(g13,g1)
    c: PointOnObject(g13,g3)
    c: Vertical(g13)
    c: Equal(g13,g12)
    c: Vertical(g6,g0)
    c: Vertical(g5,g0)
    c: Vertical(g10,g2)
    c: Vertical(g9,g1)
FEATURE [PartDesign::Pocket] Pocket013
  AddSubType = 1
  AutoTaperInnerAngle = true
  BaseFeature = -> Pad009
  CheckUpToFaceLimits = true
  ClaimChildren = false
  Direction = (-1,2e-16,-3e-16)
  Fit = 0
  FitJoin = 0
  InnerFit = 0
  InnerFitJoin = 0
  InvalidShape = false
  Length = 5
  Length2 = 100
  Linearize = true
  NewSolid = false
  Profile = -> Sketch025
  Refine = true
  Reversed = true
  Suppress = false
  TaperInnerAngle = 0
  TaperInnerAngleRev = 0
  TreeRank = 250
  Type = 1
  ValidateShape = true
  _ProfileBasedVersion = 1
  _Version = 1
FEATURE [Sketcher::SketchObject] Sketch026
  ArcFitTolerance = 1e-06
  AttachmentSupport = -> [XZ_Plane012]
  ExternalBSplineMaxDegree = 5
  ExternalBSplineTolerance = 0.0001
  FullyConstrained = true
  InternalTolerance = 1e-06
  InvalidShape = false
  MakeInternals = true
  MapMode = 5
  Placement = pos=(0,0,0) rot=(1,0,0;1.5708rad)
  Support = -> [XZ_Plane012]
  TreeRank = 251
  ValidateShape = true
  sketch-geometry (4):
    g0: LineSegment StartX=-135.779 StartY=2.0606e-12 StartZ=0 EndX=-128.5 EndY=20 EndZ=0
    g1: LineSegment StartX=-128.5 StartY=20 StartZ=0 EndX=128.5 EndY=20 EndZ=0
    g2: LineSegment StartX=128.5 StartY=20 StartZ=0 EndX=135.779 EndY=-4.7216e-12 EndZ=0
    g3: LineSegment StartX=135.779 StartY=-4.7225e-12 StartZ=0 EndX=-135.779 EndY=2.0606e-12 EndZ=0
  constraints (10):
    c: PointOnObject(g0,g-1)
    c: Coincident(g0,g1)
    c: Coincident(g1,g2)
    c: Coincident(g2,g3)
    c: Coincident(g3,g0)
    c: Symmetric(g0,g2,g-1)
    c: Symmetric(g1,g0,g-2)
    c: DistanceX(g1,g1) = 257
    c: Angle(g2,g3) = 1.22173
    c: DistanceY(g-1,g1) = 20
FEATURE [PartDesign::Pocket] Pocket014
  AddSubType = 1
  AutoTaperInnerAngle = true
  BaseFeature = -> Pad011
  CheckUpToFaceLimits = true
  ClaimChildren = false
  Direction = (1,1,1)
  Fit = 0
  FitJoin = 0
  InnerFit = 0
  InnerFitJoin = 0
  InvalidShape = false
  Length = 5
  Length2 = 100
  Linearize = true
  NewSolid = false
  Profile = -> Sketch026
  Refine = true
  Reversed = true
  Suppress = false
  TaperInnerAngle = 0
  TaperInnerAngleRev = 0
  TreeRank = 252
  Type = 1
  ValidateShape = true
  _ProfileBasedVersion = 1
  _Version = 1
FEATURE [Sketcher::SketchObject] Sketch028
  ArcFitTolerance = 1e-06
  AttachmentOffset = pos=(0,0,30) rot=(0,0,1;0rad)
  AttachmentSupport = -> [XY_Plane008]
  ExternalBSplineMaxDegree = 5
  ExternalBSplineTolerance = 0.0001
  ExternalGeometry = -> [Pad008]
  FullyConstrained = true
  InternalTolerance = 1e-06
  InvalidShape = false
  MakeInternals = true
  MapMode = 5
  Placement = pos=(0,0,30) rot=(0,0,1;0rad)
  Support = -> [XY_Plane008]
  TreeRank = 255
  ValidateShape = true
  sketch-geometry (32):
    g0: LineSegment StartX=-90 StartY=120 StartZ=0 EndX=-30 EndY=120 EndZ=0
    g1: LineSegment StartX=-30 StartY=120 StartZ=0 EndX=-30 EndY=130 EndZ=0
    g2: LineSegment StartX=-30 StartY=130 StartZ=0 EndX=-90 EndY=130 EndZ=0
    g3: LineSegment StartX=-90 StartY=130 StartZ=0 EndX=-90 EndY=120 EndZ=0
    g4: LineSegment StartX=30 StartY=120 StartZ=0 EndX=90 EndY=120 EndZ=0
    g5: LineSegment StartX=90 StartY=120 StartZ=0 EndX=90 EndY=130 EndZ=0
    g6: LineSegment StartX=90 StartY=130 StartZ=0 EndX=30 EndY=130 EndZ=0
    g7: LineSegment StartX=30 StartY=130 StartZ=0 EndX=30 EndY=120 EndZ=0
    g8: LineSegment StartX=-165 StartY=90 StartZ=0 EndX=-175 EndY=90 EndZ=0
    g9: LineSegment StartX=-175 StartY=90 StartZ=0 EndX=-175 EndY=30 EndZ=0
    g10: LineSegment StartX=-175 StartY=30 StartZ=0 EndX=-165 EndY=30 EndZ=0
    g11: LineSegment StartX=-165 StartY=30 StartZ=0 EndX=-165 EndY=90 EndZ=0
    g12: LineSegment StartX=-165 StartY=-30 StartZ=0 EndX=-175 EndY=-30 EndZ=0
    g13: LineSegment StartX=-175 StartY=-30 StartZ=0 EndX=-175 EndY=-90 EndZ=0
    g14: LineSegment StartX=-175 StartY=-90 StartZ=0 EndX=-165 EndY=-90 EndZ=0
    g15: LineSegment StartX=-165 StartY=-90 StartZ=0 EndX=-165 EndY=-30 EndZ=0
    g16: LineSegment StartX=-90 StartY=-120 StartZ=0 EndX=-30 EndY=-120 EndZ=0
    g17: LineSegment StartX=-30 StartY=-120 StartZ=0 EndX=-30 EndY=-130 EndZ=0
    g18: LineSegment StartX=-30 StartY=-130 StartZ=0 EndX=-90 EndY=-130 EndZ=0
    g19: LineSegment StartX=-90 StartY=-130 StartZ=0 EndX=-90 EndY=-120 EndZ=0
    g20: LineSegment StartX=30 StartY=-120 StartZ=0 EndX=90 EndY=-120 EndZ=0
    g21: LineSegment StartX=90 StartY=-120 StartZ=0 EndX=90 EndY=-130 EndZ=0
    g22: LineSegment StartX=90 StartY=-130 StartZ=0 EndX=30 EndY=-130 EndZ=0
    g23: LineSegment StartX=30 StartY=-130 StartZ=0 EndX=30 EndY=-120 EndZ=0
    g24: LineSegment StartX=165 StartY=-90 StartZ=0 EndX=175 EndY=-90 EndZ=0
    g25: LineSegment StartX=175 StartY=-90 StartZ=0 EndX=175 EndY=-30 EndZ=0
    g26: LineSegment StartX=175 StartY=-30 StartZ=0 EndX=165 EndY=-30 EndZ=0
    g27: LineSegment StartX=165 StartY=-30 StartZ=0 EndX=165 EndY=-90 EndZ=0
    g28: LineSegment StartX=165 StartY=30 StartZ=0 EndX=175 EndY=30 EndZ=0
    g29: LineSegment StartX=175 StartY=30 StartZ=0 EndX=175 EndY=90 EndZ=0
    g30: LineSegment StartX=175 StartY=90 StartZ=0 EndX=165 EndY=90 EndZ=0
    g31: LineSegment StartX=165 StartY=90 StartZ=0 EndX=165 EndY=30 EndZ=0
  constraints (90):
    c: Coincident(g0,g1)
    c: Coincident(g1,g2)
    c: Coincident(g2,g3)
    c: Coincident(g3,g0)
    c: Horizontal(g0)
    c: Horizontal(g2)
    c: Vertical(g1)
    c: Vertical(g3)
    c: PointOnObject(g0,g-3)
    c: DistanceY(g3,g3) = 10
    c: DistanceX(g2,g2) = 60
    c: Coincident(g4,g5)
    c: Coincident(g5,g6)
    c: Coincident(g6,g7)
    c: Coincident(g7,g4)
    c: Horizontal(g4)
    c: Horizontal(g6)
    c: Vertical(g5)
    c: Vertical(g7)
    c: PointOnObject(g4,g-3)
    c: Coincident(g8,g9)
    c: Coincident(g9,g10)
    c: Coincident(g10,g11)
    c: Coincident(g11,g8)
    c: Horizontal(g8)
    c: Horizontal(g10)
    c: Vertical(g9)
    c: Vertical(g11)
    c: PointOnObject(g8,g-4)
    c: Coincident(g12,g13)
    c: Coincident(g13,g14)
    c: Coincident(g14,g15)
    c: Coincident(g15,g12)
    c: Horizontal(g12)
    c: Horizontal(g14)
    c: Vertical(g13)
    c: Vertical(g15)
    c: PointOnObject(g12,g-4)
    c: Coincident(g16,g17)
    c: Coincident(g17,g18)
    c: Coincident(g18,g19)
    c: Coincident(g19,g16)
    c: Horizontal(g16)
    c: Horizontal(g18)
    c: Vertical(g17)
    c: Vertical(g19)
    c: Coincident(g20,g21)
    c: Coincident(g21,g22)
    c: Coincident(g22,g23)
    c: Coincident(g23,g20)
    c: Horizontal(g20)
    c: Horizontal(g22)
    c: Vertical(g21)
    c: Vertical(g23)
    c: PointOnObject(g20,g-5)
    c: Coincident(g24,g25)
    c: Coincident(g25,g26)
    c: Coincident(g26,g27)
    c: Coincident(g27,g24)
    c: Horizontal(g24)
    c: Horizontal(g26)
    c: Vertical(g25)
    c: Vertical(g27)
    c: Coincident(g28,g29)
    c: Coincident(g29,g30)
    c: Coincident(g30,g31)
    c: Coincident(g31,g28)
    c: Horizontal(g28)
    c: Horizontal(g30)
    c: Vertical(g29)
    c: Vertical(g31)
    c: Equal(g1,g8)
    c: Equal(g12,g19)
    c: Equal(g23,g26)
    c: Equal(g26,g28)
    c: Equal(g9,g2)
    c: Equal(g2,g6)
    c: Equal(g6,g29)
    c: Equal(g29,g25)
    c: Equal(g25,g22)
    c: Equal(g22,g18)
    c: Equal(g18,g13)
    c: Symmetric(g6,g1,g-2)
    c: Symmetric(g9,g12,g-1)
    c: Symmetric(g17,g22,g-2)
    c: Symmetric(g26,g28,g-1)
    c: Symmetric(g0,g16,g-1)
    c: Symmetric(g10,g28,g-2)
    c: DistanceY(g12,g9) = 60
    c: DistanceX(g1,g6) = 60
FEATURE [PartDesign::Pad] Pad012
  AddSubType = 0
  AlongSketchNormal = false
  AutoTaperInnerAngle = true
  BaseFeature = -> Pad008
  CheckUpToFaceLimits = true
  ClaimChildren = false
  Direction = (0,0,1)
  Fit = 0
  FitJoin = 0
  InnerFit = 0
  InnerFitJoin = 0
  InvalidShape = false
  Length = 10
  Length2 = 100
  Linearize = true
  NewSolid = false
  Profile = -> Sketch028
  Refine = true
  Suppress = false
  TaperInnerAngle = 0
  TaperInnerAngleRev = 0
  TreeRank = 256
  Type = 0
  ValidateShape = true
  _ProfileBasedVersion = 1
FEATURE [PartDesign::Fillet] Fillet009
  AddSubType = 0
  Base = -> Pad012 [Edge56,Edge2,Edge87,Edge27]
  BaseFeature = -> Pad012
  InvalidShape = false
  NewSolid = false
  Radius = 10
  Refine = true
  SupportTransform = false
  Suppress = false
  TreeRank = 257
  UseAllEdges = false
  ValidateShape = true
FEATURE [PartDesign::Chamfer] Chamfer026
  AddSubType = 0
  Angle = 45
  Base = -> Fillet009 [Edge108,Edge110,Edge116,Edge46,Edge119,Edge118,Edge113,Edge111,Edge101,Edge99,Edge91,Edge93,Edge88,Edge90,Edge98,Edge96]
  BaseFeature = -> Fillet009
  ChamferType = 0
  FlipDirection = false
  InvalidShape = false
  NewSolid = false
  Refine = true
  Size = 3
  Size2 = 1
  SupportTransform = false
  Suppress = false
  TreeRank = 258
  UseAllEdges = false
  ValidateShape = true
FEATURE [PartDesign::Body] Body007  label="BottomPart"
  AutoGroupSolids = false
  ClaimAllChildren = false
  ExportMode = 0
  Group = -> [Import,Sketch021,Pad008,Sketch028,Pad012,Fillet009,Chamfer026]
  InvalidShape = false
  Origin = -> Origin010
  SingleSolid = true
  Tip = -> Chamfer026
  TreeRank = 197
  ValidateShape = true
  _ExportChildren = -> [Import,Pad008,Pad012,Fillet009,Chamfer026]
  _GroupVersion = 1
FEATURE [Part::SubShapeBinder] Import002  label="Import002(Chamfer026)"
  BindCopyOnChange = 0
  BindMode = 0
  ClaimChildren = false
  Context = -> Part001 [Body008.Import002.]
  EdgeTolerance = 1e-06
  FillStyle = 0
  Fuse = false
  InvalidShape = false
  MakeFace = false
  MergeEdges = true
  OffsetFill = false
  OffsetIntersection = false
  OffsetJoinType = 0
  OffsetOpenResult = false
  Outline = false
  PartialLoad = false
  Relative = true
  SplitEdges = false
  Support = -> [Body007[Chamfer026.]]
  TightBound = false
  TreeRank = 260
  ValidateShape = true
  _Version = 8
FEATURE [Sketcher::SketchObject] Sketch029
  ArcFitTolerance = 1e-06
  AttachmentSupport = -> [YZ_Plane009]
  ExternalBSplineMaxDegree = 5
  ExternalBSplineTolerance = 0.0001
  ExternalGeometry = -> [Import002]
  FullyConstrained = true
  InternalTolerance = 1e-06
  InvalidShape = false
  MakeInternals = true
  MapMode = 5
  Placement = pos=(0,0,0) rot=(0.57735,0.57735,0.57735;2.0944rad)
  Support = -> [YZ_Plane009]
  TreeRank = 259
  ValidateShape = true
  sketch-geometry (8):
    g0: LineSegment StartX=-90 StartY=40 StartZ=0 EndX=-30 EndY=40 EndZ=0
    g1: LineSegment StartX=-30 StartY=40 StartZ=0 EndX=-30 EndY=30 EndZ=0
    g2: LineSegment StartX=-30 StartY=30 StartZ=0 EndX=-90 EndY=30 EndZ=0
    g3: LineSegment StartX=-90 StartY=30 StartZ=0 EndX=-90 EndY=40 EndZ=0
    g4: LineSegment StartX=30 StartY=40 StartZ=0 EndX=90 EndY=40 EndZ=0
    g5: LineSegment StartX=90 StartY=40 StartZ=0 EndX=90 EndY=30 EndZ=0
    g6: LineSegment StartX=90 StartY=30 StartZ=0 EndX=30 EndY=30 EndZ=0
    g7: LineSegment StartX=30 StartY=30 StartZ=0 EndX=30 EndY=40 EndZ=0
  constraints (20):
    c: Coincident(g0,g1)
    c: Coincident(g1,g2)
    c: Coincident(g2,g3)
    c: Coincident(g3,g0)
    c: Horizontal(g0)
    c: Horizontal(g2)
    c: Vertical(g1)
    c: Vertical(g3)
    c: Coincident(g0,g-3)
    c: Coincident(g1,g-5)
    c: Coincident(g4,g5)
    c: Coincident(g5,g6)
    c: Coincident(g6,g7)
    c: Coincident(g7,g4)
    c: Horizontal(g4)
    c: Horizontal(g6)
    c: Vertical(g5)
    c: Vertical(g7)
    c: Coincident(g4,g-6)
    c: Coincident(g5,g-4)
FEATURE [PartDesign::Pocket] Pocket016
  AddSubType = 1
  AutoTaperInnerAngle = true
  BaseFeature = -> Pocket013
  CheckUpToFaceLimits = true
  ClaimChildren = false
  Direction = (-1,2e-16,-3e-16)
  Fit = 0
  FitJoin = 0
  InnerFit = 0
  InnerFitJoin = 0
  InvalidShape = false
  Length = 5
  Length2 = 100
  Linearize = true
  NewSolid = false
  Profile = -> Sketch029
  Refine = true
  Reversed = true
  Suppress = false
  TaperInnerAngle = 0
  TaperInnerAngleRev = 0
  TreeRank = 261
  Type = 1
  ValidateShape = true
  _ProfileBasedVersion = 1
  _Version = 1
FEATURE [Part::SubShapeBinder] Import003  label="Import003(Chamfer026)"
  BindCopyOnChange = 0
  BindMode = 0
  ClaimChildren = false
  Context = -> Part001 [Body011.Import003.]
  EdgeTolerance = 1e-06
  FillStyle = 0
  Fuse = false
  InvalidShape = false
  MakeFace = false
  MergeEdges = true
  OffsetFill = false
  OffsetIntersection = false
  OffsetJoinType = 0
  OffsetOpenResult = false
  Outline = false
  PartialLoad = false
  Relative = true
  SplitEdges = false
  Support = -> [Body007[Chamfer026.]]
  TightBound = false
  TreeRank = 263
  ValidateShape = true
  _Version = 8
FEATURE [Sketcher::SketchObject] Sketch030
  ArcFitTolerance = 1e-06
  AttachmentSupport = -> [XZ_Plane012]
  ExternalBSplineMaxDegree = 5
  ExternalBSplineTolerance = 0.0001
  ExternalGeometry = -> [Import003]
  FullyConstrained = true
  InternalTolerance = 1e-06
  InvalidShape = false
  MakeInternals = true
  MapMode = 5
  Placement = pos=(0,0,0) rot=(1,0,0;1.5708rad)
  Support = -> [XZ_Plane012]
  TreeRank = 262
  ValidateShape = true
  sketch-geometry (8):
    g0: LineSegment StartX=90 StartY=40 StartZ=0 EndX=30 EndY=40 EndZ=0
    g1: LineSegment StartX=30 StartY=40 StartZ=0 EndX=30 EndY=30 EndZ=0
    g2: LineSegment StartX=30 StartY=30 StartZ=0 EndX=90 EndY=30 EndZ=0
    g3: LineSegment StartX=90 StartY=30 StartZ=0 EndX=90 EndY=40 EndZ=0
    g4: LineSegment StartX=-30 StartY=40 StartZ=0 EndX=-90 EndY=40 EndZ=0
    g5: LineSegment StartX=-90 StartY=40 StartZ=0 EndX=-90 EndY=30 EndZ=0
    g6: LineSegment StartX=-90 StartY=30 StartZ=0 EndX=-30 EndY=30 EndZ=0
    g7: LineSegment StartX=-30 StartY=30 StartZ=0 EndX=-30 EndY=40 EndZ=0
  constraints (20):
    c: Coincident(g0,g1)
    c: Coincident(g1,g2)
    c: Coincident(g2,g3)
    c: Coincident(g3,g0)
    c: Horizontal(g0)
    c: Horizontal(g2)
    c: Vertical(g1)
    c: Vertical(g3)
    c: Coincident(g0,g-3)
    c: Coincident(g1,g-4)
    c: Coincident(g4,g5)
    c: Coincident(g5,g6)
    c: Coincident(g6,g7)
    c: Coincident(g7,g4)
    c: Horizontal(g4)
    c: Horizontal(g6)
    c: Vertical(g5)
    c: Vertical(g7)
    c: Coincident(g4,g-5)
    c: Coincident(g5,g-6)
FEATURE [PartDesign::Pocket] Pocket017
  AddSubType = 1
  AutoTaperInnerAngle = true
  BaseFeature = -> Pocket014
  CheckUpToFaceLimits = true
  ClaimChildren = false
  Direction = (0,1,2e-16)
  Fit = 0
  FitJoin = 0
  InnerFit = 0
  InnerFitJoin = 0
  InvalidShape = false
  Length = 5
  Length2 = 100
  Linearize = true
  NewSolid = false
  Profile = -> Sketch030
  Refine = true
  Reversed = true
  Suppress = false
  TaperInnerAngle = 0
  TaperInnerAngleRev = 0
  TreeRank = 264
  Type = 1
  ValidateShape = true
  _ProfileBasedVersion = 1
  _Version = 1
FEATURE [Sketcher::SketchObject] Sketch031
  ArcFitTolerance = 1e-06
  AttachmentSupport = -> [XZ_Plane012]
  ExternalBSplineMaxDegree = 5
  ExternalBSplineTolerance = 0.0001
  ExternalGeometry = -> [Pocket017]
  FullyConstrained = true
  InternalTolerance = 1e-06
  InvalidShape = false
  MakeInternals = true
  MapMode = 5
  Placement = pos=(0,0,0) rot=(1,0,0;1.5708rad)
  Support = -> [XZ_Plane012]
  TreeRank = 265
  ValidateShape = true
  sketch-geometry (8):
    g0: LineSegment StartX=165 StartY=185 StartZ=0 EndX=175 EndY=185 EndZ=0
    g1: LineSegment StartX=175 StartY=185 StartZ=0 EndX=175 EndY=125 EndZ=0
    g2: LineSegment StartX=175 StartY=125 StartZ=0 EndX=165 EndY=125 EndZ=0
    g3: LineSegment StartX=165 StartY=125 StartZ=0 EndX=165 EndY=185 EndZ=0
    g4: LineSegment StartX=-165 StartY=185 StartZ=0 EndX=-175 EndY=185 EndZ=0
    g5: LineSegment StartX=-175 StartY=185 StartZ=0 EndX=-175 EndY=125 EndZ=0
    g6: LineSegment StartX=-175 StartY=125 StartZ=0 EndX=-165 EndY=125 EndZ=0
    g7: LineSegment StartX=-165 StartY=125 StartZ=0 EndX=-165 EndY=185 EndZ=0
  constraints (23):
    c: Coincident(g0,g1)
    c: Coincident(g1,g2)
    c: Coincident(g2,g3)
    c: Coincident(g3,g0)
    c: Horizontal(g0)
    c: Horizontal(g2)
    c: Vertical(g1)
    c: Vertical(g3)
    c: PointOnObject(g0,g-3)
    c: Coincident(g4,g5)
    c: Coincident(g5,g6)
    c: Coincident(g6,g7)
    c: Coincident(g7,g4)
    c: Horizontal(g4)
    c: Horizontal(g6)
    c: Vertical(g5)
    c: Vertical(g7)
    c: Equal(g5,g1)
    c: Equal(g0,g4)
    c: DistanceX(g0,g0) = 10
    c: DistanceY(g1,g1) = 60
    c: DistanceY(g0,g-3) = 30
    c: Symmetric(g4,g0,g-2)
FEATURE [PartDesign::Pad] Pad013
  AddSubType = 0
  AlongSketchNormal = false
  AutoTaperInnerAngle = true
  BaseFeature = -> Pocket017
  CheckUpToFaceLimits = true
  ClaimChildren = false
  Direction = (0,-1,-2e-16)
  Fit = 0
  FitJoin = 0
  InnerFit = 0
  InnerFitJoin = 0
  InvalidShape = false
  Length = 10
  Length2 = 100
  Linearize = true
  NewSolid = false
  Profile = -> Sketch031
  Refine = true
  Suppress = false
  TaperInnerAngle = 0
  TaperInnerAngleRev = 0
  TreeRank = 266
  Type = 0
  ValidateShape = true
  _ProfileBasedVersion = 1
FEATURE [PartDesign::Chamfer] Chamfer027
  AddSubType = 0
  Angle = 45
  Base = -> Pad013 [Edge44,Edge41,Edge14,Edge5]
  BaseFeature = -> Pad013
  ChamferType = 0
  FlipDirection = false
  InvalidShape = false
  NewSolid = false
  Refine = true
  Size = 3
  Size2 = 1
  SupportTransform = false
  Suppress = false
  TreeRank = 267
  UseAllEdges = false
  ValidateShape = true
FEATURE [PartDesign::Fillet] Fillet010
  AddSubType = 0
  Base = -> Chamfer027 [Edge64,Edge35,Edge68,Edge69,Edge71,Edge76,Edge75,Edge73]
  BaseFeature = -> Chamfer027
  InvalidShape = false
  NewSolid = false
  Radius = 10
  Refine = true
  SupportTransform = false
  Suppress = false
  TreeRank = 268
  UseAllEdges = false
  ValidateShape = true
FEATURE [PartDesign::FeatureBase] Clone001
  BaseFeature = -> Chamfer027
  InvalidShape = false
  NewSolid = false
  Suppress = false
  TreeRank = 278
  ValidateShape = true
FEATURE [Sketcher::SketchObject] Sketch032
  ArcFitTolerance = 1e-06
  AttachmentSupport = -> [XZ_Plane013]
  ExternalBSplineMaxDegree = 5
  ExternalBSplineTolerance = 0.0001
  FullyConstrained = true
  InternalTolerance = 1e-06
  InvalidShape = false
  MakeInternals = true
  MapMode = 5
  Placement = pos=(0,0,0) rot=(1,0,0;1.5708rad)
  Support = -> [XZ_Plane013]
  TreeRank = 280
  ValidateShape = true
  sketch-geometry (5):
    g0: LineSegment StartX=-165 StartY=11 StartZ=0 EndX=-165 EndY=7.407e-13 EndZ=0
    g1: LineSegment StartX=-165 StartY=7.407e-13 StartZ=0 EndX=165 EndY=7.407e-13 EndZ=0
    g2: LineSegment StartX=165 StartY=7.407e-13 StartZ=0 EndX=165 EndY=11 EndZ=0
    g3: LineSegment StartX=165 StartY=11 StartZ=0 EndX=-165 EndY=11 EndZ=0
    g4: GeomPoint [constr] X=-2.4646e-12 Y=5.5 Z=0
  constraints (13):
    c: Coincident(g0,g1)
    c: Coincident(g1,g2)
    c: Coincident(g2,g3)
    c: Coincident(g3,g0)
    c: Horizontal(g1)
    c: Horizontal(g3)
    c: Vertical(g0)
    c: Vertical(g2)
    c: Symmetric(g1,g0,g4)
    c: PointOnObject(g4,g-2)
    c: DistanceX(g1,g1) = 330
    c: PointOnObject(g1,g-1)
    c: DistanceY(g2,g2) = 11
FEATURE [PartDesign::Pocket] Pocket018
  AddSubType = 1
  AutoTaperInnerAngle = true
  BaseFeature = -> Clone001
  CheckUpToFaceLimits = true
  ClaimChildren = false
  Direction = (0,1,0)
  Fit = 0
  FitJoin = 0
  InnerFit = 0
  InnerFitJoin = 0
  InvalidShape = false
  Length = 5
  Length2 = 100
  Linearize = true
  NewSolid = false
  Profile = -> Sketch032
  Refine = true
  Reversed = true
  Suppress = false
  TaperInnerAngle = 0
  TaperInnerAngleRev = 0
  TreeRank = 281
  Type = 1
  ValidateShape = true
  _ProfileBasedVersion = 1
  _Version = 1
FEATURE [Sketcher::SketchObject] Sketch033
  ArcFitTolerance = 1e-06
  AttachmentSupport = -> [XZ_Plane013]
  ExternalBSplineMaxDegree = 5
  ExternalBSplineTolerance = 0.0001
  ExternalGeometry = -> [Pocket018]
  FullyConstrained = true
  InternalTolerance = 1e-06
  InvalidShape = false
  MakeInternals = true
  MapMode = 5
  Placement = pos=(0,0,0) rot=(1,0,0;1.5708rad)
  Support = -> [XZ_Plane013]
  TreeRank = 282
  ValidateShape = true
  sketch-geometry (4):
    g0: LineSegment StartX=-165 StartY=215 StartZ=0 EndX=165 EndY=215 EndZ=0
    g1: LineSegment StartX=165 StartY=215 StartZ=0 EndX=165 EndY=230 EndZ=0
    g2: LineSegment StartX=165 StartY=230 StartZ=0 EndX=-165 EndY=230 EndZ=0
    g3: LineSegment StartX=-165 StartY=230 StartZ=0 EndX=-165 EndY=215 EndZ=0
  constraints (10):
    c: Coincident(g0,g1)
    c: Coincident(g1,g2)
    c: Coincident(g2,g3)
    c: Coincident(g3,g0)
    c: Horizontal(g2)
    c: Vertical(g1)
    c: Vertical(g3)
    c: Coincident(g0,g-3)
    c: Coincident(g-3,g0)
    c: DistanceY(g1,g1) = 15
FEATURE [PartDesign::Pad] Pad014
  AddSubType = 0
  AlongSketchNormal = false
  AutoTaperInnerAngle = true
  BaseFeature = -> Pocket018
  CheckUpToFaceLimits = true
  ClaimChildren = false
  Direction = (0,-1,-2e-16)
  Fit = 0
  FitJoin = 0
  InnerFit = 0
  InnerFitJoin = 0
  InvalidShape = false
  Length = 10
  Length2 = 100
  Linearize = true
  NewSolid = false
  Profile = -> Sketch033
  Refine = true
  Suppress = false
  TaperInnerAngle = 0
  TaperInnerAngleRev = 0
  TreeRank = 283
  Type = 0
  ValidateShape = true
  _ProfileBasedVersion = 1
FEATURE [TechDraw::DrawSVGTemplate] Template
  Height = 297
  Orientation = 1
  TreeRank = 290
  Width = 420
FEATURE [TechDraw::DrawSVGTemplate] Template001
  Height = 297
  Orientation = 1
  TreeRank = 299
  Width = 420
FEATURE [TechDraw::DrawProjGroupItem] ProjItem002  label="Front003"
  CoarseView = false
  Direction = (0,0,1)
  Focus = 100
  HardHidden = false
  IsoCount = 0
  IsoHidden = false
  IsoVisible = false
  LockPosition = true
  Perspective = false
  Rotation = 0
  RotationVector = (1,0,0)
  ScaleType = 2
  ScrubCount = 0
  SeamHidden = false
  SeamVisible = true
  SmoothHidden = false
  SmoothVisible = true
  Source = -> [Chamfer026]
  TreeRank = 302
  Type = 0
  X = 0
  XDirection = (1,0,0)
  Y = 0
FEATURE [TechDraw::DrawProjGroup] ProjGroup002
  Anchor = -> ProjItem002
  AutoDistribute = true
  LockPosition = false
  ProjectionType = 0
  Rotation = 0
  ScaleType = 0
  Source = -> [Chamfer026]
  TreeRank = 303
  Views = -> [ProjItem002]
  X = 210
  Y = 148.5
  spacingX = 15
  spacingY = 15
FEATURE [TechDraw::DrawSVGTemplate] Template002
  Height = 297
  Orientation = 1
  TreeRank = 305
  Width = 420
FEATURE [TechDraw::DrawSVGTemplate] Template003
  Height = 297
  Orientation = 1
  TreeRank = 311
  Width = 420
FEATURE [App::Link] Link  label="Link(Hinge)"
  AutoLinkLabel = true
  AutoPlacement = true
  LinkPlacement = pos=(-115,115,225) rot=(0.57735,-0.57735,0.57735;4.18879rad)
  LinkedObject = -> Part
  Placement = pos=(-115,115,225) rot=(0.57735,-0.57735,0.57735;4.18879rad)
  SyncGroupVisibility = false
  TreeRank = 318
  _LinkVersion = 1
FEATURE [App::Link] Link001  label="Link001(*Hinge)"
  AutoLinkLabel = true
  AutoPlacement = true
  LinkPlacement = pos=(115,115,225) rot=(0.57735,-0.57735,0.57735;4.18879rad)
  LinkedObject = -> Link
  Placement = pos=(115,115,225) rot=(0.57735,-0.57735,0.57735;4.18879rad)
  SyncGroupVisibility = false
  TreeRank = 320
  _LinkVersion = 1
FEATURE [Part::SubShapeBinder] Import004  label="Import004(Fillet013)"
  BindCopyOnChange = 0
  BindMode = 0
  ClaimChildren = false
  Context = -> Part001 [Body008.Import004.]
  EdgeTolerance = 1e-06
  FillStyle = 0
  Fuse = false
  InvalidShape = false
  MakeFace = false
  MergeEdges = true
  OffsetFill = false
  OffsetIntersection = false
  OffsetJoinType = 0
  OffsetOpenResult = false
  Outline = false
  PartialLoad = false
  Relative = true
  SplitEdges = false
  Support = -> [Body012[Fillet013.]]
  TightBound = false
  TreeRank = 322
  ValidateShape = true
  _Version = 8
FEATURE [Sketcher::SketchObject] Sketch034
  ArcFitTolerance = 1e-06
  AttachmentSupport = -> [YZ_Plane009]
  ExternalBSplineMaxDegree = 5
  ExternalBSplineTolerance = 0.0001
  ExternalGeometry = -> [Import004]
  FullyConstrained = true
  InternalTolerance = 1e-06
  InvalidShape = false
  MakeInternals = true
  MapMode = 5
  Placement = pos=(0,0,0) rot=(0.57735,0.57735,0.57735;2.0944rad)
  Support = -> [YZ_Plane009]
  TreeRank = 285
  ValidateShape = true
  sketch-geometry (8):
    g0: LineSegment StartX=-130 StartY=185 StartZ=0 EndX=-120 EndY=185 EndZ=0
    g1: LineSegment StartX=-120 StartY=185 StartZ=0 EndX=-120 EndY=125 EndZ=0
    g2: LineSegment StartX=-120 StartY=125 StartZ=0 EndX=-130 EndY=125 EndZ=0
    g3: LineSegment StartX=-130 StartY=125 StartZ=0 EndX=-130 EndY=185 EndZ=0
    g4: LineSegment StartX=120 StartY=185 StartZ=0 EndX=130 EndY=185 EndZ=0
    g5: LineSegment StartX=130 StartY=185 StartZ=0 EndX=130 EndY=125 EndZ=0
    g6: LineSegment StartX=130 StartY=125 StartZ=0 EndX=120 EndY=125 EndZ=0
    g7: LineSegment StartX=120 StartY=125 StartZ=0 EndX=120 EndY=185 EndZ=0
  constraints (20):
    c: Coincident(g0,g1)
    c: Coincident(g1,g2)
    c: Coincident(g2,g3)
    c: Coincident(g3,g0)
    c: Horizontal(g0)
    c: Horizontal(g2)
    c: Vertical(g1)
    c: Vertical(g3)
    c: Coincident(g4,g5)
    c: Coincident(g5,g6)
    c: Coincident(g6,g7)
    c: Coincident(g7,g4)
    c: Horizontal(g4)
    c: Vertical(g5)
    c: Vertical(g7)
    c: Symmetric(g6,g1,g-2)
    c: Symmetric(g5,g2,g-2)
    c: Equal(g7,g1)
    c: Coincident(g-4,g1)
    c: Coincident(g0,g-3)
FEATURE [PartDesign::Pocket] Pocket019
  AddSubType = 1
  AutoTaperInnerAngle = true
  BaseFeature = -> Pocket016
  CheckUpToFaceLimits = true
  ClaimChildren = false
  Direction = (-1,2e-16,-3e-16)
  Fit = 0
  FitJoin = 0
  InnerFit = 0
  InnerFitJoin = 0
  InvalidShape = false
  Length = 5
  Length2 = 100
  Linearize = true
  NewSolid = false
  Profile = -> Sketch034
  Refine = true
  Reversed = true
  Suppress = false
  TaperInnerAngle = 0
  TaperInnerAngleRev = 0
  TreeRank = 287
  Type = 1
  ValidateShape = true
  _ProfileBasedVersion = 1
  _Version = 1
FEATURE [PartDesign::Fillet] Fillet012
  AddSubType = 0
  Base = -> Pocket019 [Edge64,Edge66,Edge68,Edge67,Edge65,Edge63,Edge61,Edge4,Edge60,Edge2,Edge32,Edge62]
  BaseFeature = -> Pocket019
  InvalidShape = false
  NewSolid = false
  Radius = 10
  Refine = true
  SupportTransform = false
  Suppress = false
  TreeRank = 288
  UseAllEdges = false
  ValidateShape = true
FEATURE [Sketcher::SketchObject] Sketch035
  ArcFitTolerance = 1e-06
  AttachmentSupport = -> [XY_Plane014]
  ExternalBSplineMaxDegree = 5
  ExternalBSplineTolerance = 0.0001
  FullyConstrained = true
  InternalTolerance = 1e-06
  InvalidShape = false
  MakeInternals = true
  MapMode = 5
  Support = -> [XY_Plane014]
  TreeRank = 333
  ValidateShape = true
  sketch-geometry (5):
    g0: LineSegment StartX=-164 StartY=-130 StartZ=0 EndX=-164 EndY=115 EndZ=0
    g1: LineSegment StartX=-164 StartY=115 StartZ=0 EndX=164 EndY=115 EndZ=0
    g2: LineSegment StartX=164 StartY=115 StartZ=0 EndX=164 EndY=-130 EndZ=0
    g3: LineSegment StartX=164 StartY=-130 StartZ=0 EndX=-164 EndY=-130 EndZ=0
    g4: GeomPoint [constr] X=-1.57124e-11 Y=-7.5 Z=0
  constraints (13):
    c: Coincident(g0,g1)
    c: Coincident(g1,g2)
    c: Coincident(g2,g3)
    c: Coincident(g3,g0)
    c: Horizontal(g1)
    c: Horizontal(g3)
    c: Vertical(g0)
    c: Vertical(g2)
    c: Symmetric(g1,g0,g4)
    c: PointOnObject(g4,g-2)
    c: DistanceX(g1,g1) = 328
    c: DistanceY(g4,g-1) = 7.5
    c: DistanceY(g2,g2) = 245
FEATURE [PartDesign::Pad] Pad015
  AddSubType = 0
  AlongSketchNormal = false
  AutoTaperInnerAngle = true
  CheckUpToFaceLimits = true
  ClaimChildren = false
  Direction = (0,0,1)
  Fit = 0
  FitJoin = 0
  InnerFit = 0
  InnerFitJoin = 0
  InvalidShape = false
  Length = 3
  Length2 = 100
  Linearize = true
  NewSolid = false
  Profile = -> Sketch035
  Refine = true
  Suppress = false
  TaperInnerAngle = 0
  TaperInnerAngleRev = 0
  TreeRank = 336
  Type = 0
  ValidateShape = true
  _ProfileBasedVersion = 1
FEATURE [Part::SubShapeBinder] Import005  label="Import005(Fillet006)"
  BindCopyOnChange = 0
  BindMode = 0
  ClaimChildren = false
  Context = -> Part001 [Group003.Body013.Import005.]
  EdgeTolerance = 1e-06
  FillStyle = 0
  Fuse = false
  InvalidShape = false
  MakeFace = false
  MergeEdges = true
  OffsetFill = false
  OffsetIntersection = false
  OffsetJoinType = 0
  OffsetOpenResult = false
  Outline = false
  PartialLoad = false
  Relative = true
  SplitEdges = false
  Support = -> [Link[Body004.Fillet006.]]
  TightBound = false
  TreeRank = 338
  ValidateShape = true
  _Version = 8
FEATURE [Part::SubShapeBinder] Import006  label="Import006(Fillet006)"
  BindCopyOnChange = 0
  BindMode = 0
  ClaimChildren = false
  Context = -> Part001 [Group003.Body013.Import006.]
  EdgeTolerance = 1e-06
  FillStyle = 0
  Fuse = false
  InvalidShape = false
  MakeFace = false
  MergeEdges = true
  OffsetFill = false
  OffsetIntersection = false
  OffsetJoinType = 0
  OffsetOpenResult = false
  Outline = false
  PartialLoad = false
  Relative = true
  SplitEdges = false
  Support = -> [Link001[Body004.Fillet006.]]
  TightBound = false
  TreeRank = 339
  ValidateShape = true
  _Version = 8
FEATURE [Sketcher::SketchObject] Sketch036
  ArcFitTolerance = 1e-06
  AttachmentSupport = -> [XY_Plane014]
  ExternalBSplineMaxDegree = 5
  ExternalBSplineTolerance = 0.0001
  ExternalGeometry = -> [Import005,Import006]
  FullyConstrained = true
  InternalTolerance = 1e-06
  InvalidShape = false
  MakeInternals = true
  MapMode = 5
  Support = -> [XY_Plane014]
  TreeRank = 337
  ValidateShape = true
  sketch-geometry (4):
    g0: Circle CenterX=-143 CenterY=102 CenterZ=0 NormalX=0 NormalY=0 NormalZ=1 AngleXU=0 Radius=1.6
    g1: Circle CenterX=-87 CenterY=102 CenterZ=0 NormalX=0 NormalY=0 NormalZ=1 AngleXU=0 Radius=1.6
    g2: Circle CenterX=87 CenterY=102 CenterZ=0 NormalX=0 NormalY=0 NormalZ=1 AngleXU=0 Radius=1.6
    g3: Circle CenterX=143 CenterY=102 CenterZ=0 NormalX=0 NormalY=0 NormalZ=1 AngleXU=0 Radius=1.6
  constraints (8):
    c: Coincident(g0,g-3)
    c: Coincident(g1,g-4)
    c: Coincident(g2,g-5)
    c: Coincident(g3,g-6)
    c: Equal(g3,g2)
    c: Equal(g3,g1)
    c: Equal(g3,g0)
    c: Diameter(g3) = 3.2
FEATURE [PartDesign::Pocket] Pocket020
  AddSubType = 1
  AutoTaperInnerAngle = true
  BaseFeature = -> Pad015
  CheckUpToFaceLimits = true
  ClaimChildren = false
  Direction = (0,0,-1)
  Fit = 0
  FitJoin = 0
  InnerFit = 0
  InnerFitJoin = 0
  InvalidShape = false
  Length = 5
  Length2 = 100
  Linearize = true
  NewSolid = false
  Profile = -> Sketch036
  Refine = true
  Reversed = true
  Suppress = false
  TaperInnerAngle = 0
  TaperInnerAngleRev = 0
  TreeRank = 340
  Type = 1
  ValidateShape = true
  _ProfileBasedVersion = 1
  _Version = 1
FEATURE [Part::FeaturePython] Screw  label="M3x20-Vis009"  # Fasteners workbench fastener (typed FeaturePython)
  InvalidShape = false
  Placement = pos=(143,102,233) rot=(0,0,1;0rad)
  TreeRank = 345
  ValidateShape = true
  baseObject = -> Body013 [Edge42]
  diameter = 1
  invert = true
  leftHanded = false
  length = 6
  lengthCustom = 20
  matchOuter = false
  offset = 0
  thread = false
  type = 50
FEATURE [Part::FeaturePython] Screw001  label="M3x20-Vis008"  # Fasteners workbench fastener (typed FeaturePython)
  InvalidShape = false
  Placement = pos=(87,102,233) rot=(0,0,1;0rad)
  TreeRank = 346
  ValidateShape = true
  baseObject = -> Body013 [Edge40]
  diameter = 1
  invert = true
  leftHanded = false
  length = 6
  lengthCustom = 20
  matchOuter = false
  offset = 0
  thread = false
  type = 50
FEATURE [Part::FeaturePython] Screw002  label="M3x20-Vis007"  # Fasteners workbench fastener (typed FeaturePython)
  InvalidShape = false
  Placement = pos=(-87,102,233) rot=(0,0,1;0rad)
  TreeRank = 347
  ValidateShape = true
  baseObject = -> Body013 [Edge80]
  diameter = 1
  invert = true
  leftHanded = false
  length = 6
  lengthCustom = 20
  matchOuter = false
  offset = 0
  thread = false
  type = 50
FEATURE [Part::FeaturePython] Screw003  label="M3x20-Vis"  # Fasteners workbench fastener (typed FeaturePython)
  InvalidShape = false
  Placement = pos=(-143,102,233) rot=(0,0,1;0rad)
  TreeRank = 348
  ValidateShape = true
  baseObject = -> Body013 [Edge78]
  diameter = 1
  invert = true
  leftHanded = false
  length = 6
  lengthCustom = 20
  matchOuter = false
  offset = 0
  thread = false
  type = 50
FEATURE [PartDesign::Fillet] Fillet014
  AddSubType = 0
  Base = -> Pocket020 [Edge5,Edge8,Edge2,Edge1]
  BaseFeature = -> Pocket020
  InvalidShape = false
  NewSolid = false
  Radius = 10
  Refine = true
  SupportTransform = false
  Suppress = false
  TreeRank = 349
  UseAllEdges = false
  ValidateShape = true
FEATURE [Sketcher::SketchObject] Sketch038
  ArcFitTolerance = 1e-06
  AttachmentSupport = -> [YZ_Plane009]
  ExternalBSplineMaxDegree = 5
  ExternalBSplineTolerance = 0.0001
  ExternalGeometry = -> [Fillet012]
  FullyConstrained = true
  InternalTolerance = 1e-06
  InvalidShape = false
  MakeInternals = true
  MapMode = 5
  Placement = pos=(0,0,0) rot=(0.57735,0.57735,0.57735;2.0944rad)
  Support = -> [YZ_Plane009]
  TreeRank = 353
  ValidateShape = true
  sketch-geometry (10):
    g0: ArcOfCircle CenterX=-40 CenterY=205 CenterZ=0 NormalX=0 NormalY=0 NormalZ=1 AngleXU=0 Radius=10 StartAngle=1.5708 EndAngle=3.14159
    g1: LineSegment StartX=-40 StartY=215 StartZ=0 EndX=40 EndY=215 EndZ=0
    g2: ArcOfCircle CenterX=40 CenterY=205 CenterZ=0 NormalX=0 NormalY=0 NormalZ=1 AngleXU=0 Radius=10 StartAngle=2.419e-13 EndAngle=1.5708
    g3: LineSegment StartX=50 StartY=205 StartZ=0 EndX=50 EndY=175 EndZ=0
    g4: ArcOfCircle CenterX=40 CenterY=175 CenterZ=0 NormalX=0 NormalY=0 NormalZ=1 AngleXU=0 Radius=10 StartAngle=4.71239 EndAngle=6.28319
    g5: LineSegment StartX=40 StartY=165 StartZ=0 EndX=-40 EndY=165 EndZ=0
    g6: ArcOfCircle CenterX=-40 CenterY=175 CenterZ=0 NormalX=0 NormalY=0 NormalZ=1 AngleXU=0 Radius=10 StartAngle=3.14159 EndAngle=4.71239
    g7: LineSegment StartX=-50 StartY=175 StartZ=0 EndX=-50 EndY=205 EndZ=0
    g8: GeomPoint [constr] X=-50 Y=215 Z=0
    g9: GeomPoint [constr] X=50 Y=165 Z=0
  constraints (23):
    c: Tangent(g0,g1) = 1.5708
    c: Tangent(g1,g2) = 1.5708
    c: Tangent(g2,g3) = 1.5708
    c: Tangent(g3,g4) = 1.5708
    c: Tangent(g4,g5) = 1.5708
    c: Tangent(g5,g6) = 1.5708
    c: Tangent(g6,g7) = 1.5708
    c: Tangent(g7,g0) = 1.5708
    c: Horizontal(g5)
    c: Vertical(g3)
    c: Vertical(g7)
    c: Equal(g0,g2)
    c: Equal(g2,g4)
    c: Equal(g4,g6)
    c: PointOnObject(g8,g1)
    c: PointOnObject(g8,g7)
    c: PointOnObject(g9,g3)
    c: PointOnObject(g9,g5)
    c: DistanceX(g0,g2) = 100
    c: DistanceY(g4,g1) = 50
    c: Radius(g2) = 10
    c: Symmetric(g0,g1,g-2)
    c: DistanceY(g-3,g1) = 195
FEATURE [PartDesign::Pocket] Pocket022
  AddSubType = 1
  AutoTaperInnerAngle = true
  BaseFeature = -> Fillet012
  CheckUpToFaceLimits = true
  ClaimChildren = false
  Direction = (-1,2e-16,-3e-16)
  Fit = 0
  FitJoin = 0
  InnerFit = 0
  InnerFitJoin = 0
  InvalidShape = false
  Length = 5
  Length2 = 100
  Linearize = true
  NewSolid = false
  Profile = -> Sketch038
  Refine = true
  Reversed = true
  Suppress = false
  TaperInnerAngle = 0
  TaperInnerAngleRev = 0
  TreeRank = 354
  Type = 1
  ValidateShape = true
  _ProfileBasedVersion = 1
  _Version = 1
FEATURE [PartDesign::SubShapeBinder] Binder  label="Binder(Pocket022)"
  BindCopyOnChange = 0
  BindMode = 0
  ClaimChildren = false
  Context = -> Part001 [Group006.Body014.Binder.]
  EdgeTolerance = 1e-06
  FillStyle = 0
  Fuse = false
  InvalidShape = false
  MakeFace = true
  MergeEdges = true
  OffsetFill = false
  OffsetIntersection = false
  OffsetJoinType = 0
  OffsetOpenResult = false
  Outline = false
  PartialLoad = false
  Relative = true
  SplitEdges = false
  Support = -> [Body008[Pocket022.Face5]]
  TightBound = false
  TreeRank = 365
  ValidateShape = true
  _Version = 8
FEATURE [Sketcher::SketchObject] Sketch039
  ArcFitTolerance = 1e-06
  AttachmentSupport = -> [Binder]
  ExternalBSplineMaxDegree = 5
  ExternalBSplineTolerance = 0.0001
  ExternalGeometry = -> [Binder]
  FullyConstrained = true
  InternalTolerance = 1e-06
  InvalidShape = false
  MakeInternals = true
  MapMode = 5
  Placement = pos=(175,0,3.89e-14) rot=(0.57735,0.57735,0.57735;2.0944rad)
  Support = -> [Binder]
  TreeRank = 366
  ValidateShape = true
  sketch-geometry (36):
    g0: ArcOfCircle CenterX=-40 CenterY=205 CenterZ=0 NormalX=0 NormalY=0 NormalZ=1 AngleXU=0 Radius=25 StartAngle=1.5708 EndAngle=3.14159
    g1: LineSegment StartX=-40 StartY=230 StartZ=0 EndX=40 EndY=230 EndZ=0
    g2: ArcOfCircle CenterX=40 CenterY=205 CenterZ=0 NormalX=0 NormalY=0 NormalZ=1 AngleXU=0 Radius=25 StartAngle=0 EndAngle=1.5708
    g3: LineSegment StartX=65 StartY=205 StartZ=0 EndX=65 EndY=175 EndZ=0
    g4: ArcOfCircle CenterX=40 CenterY=175 CenterZ=0 NormalX=0 NormalY=0 NormalZ=1 AngleXU=0 Radius=25 StartAngle=4.71239 EndAngle=6.28319
    g5: LineSegment StartX=40 StartY=150 StartZ=0 EndX=-40 EndY=150 EndZ=0
    g6: ArcOfCircle CenterX=-40 CenterY=175 CenterZ=0 NormalX=0 NormalY=0 NormalZ=1 AngleXU=0 Radius=25 StartAngle=3.14159 EndAngle=4.71239
    g7: LineSegment StartX=-65 StartY=175 StartZ=0 EndX=-65 EndY=205 EndZ=0
    g8: GeomPoint [constr] X=-65 Y=230 Z=0
    g9: GeomPoint [constr] X=65 Y=150 Z=0
    g10: ArcOfCircle CenterX=-40 CenterY=205 CenterZ=0 NormalX=0 NormalY=0 NormalZ=1 AngleXU=0 Radius=5 StartAngle=1.5708 EndAngle=3.14159
    g11: LineSegment StartX=-40 StartY=210 StartZ=0 EndX=40 EndY=210 EndZ=0
    g12: ArcOfCircle CenterX=40 CenterY=205 CenterZ=0 NormalX=0 NormalY=0 NormalZ=1 AngleXU=0 Radius=5 StartAngle=5e-16 EndAngle=1.5708
    g13: LineSegment StartX=45 StartY=205 StartZ=0 EndX=45 EndY=175 EndZ=0
    g14: ArcOfCircle CenterX=40 CenterY=175 CenterZ=0 NormalX=0 NormalY=0 NormalZ=1 AngleXU=0 Radius=5 StartAngle=4.71239 EndAngle=6.28319
    g15: LineSegment StartX=40 StartY=170 StartZ=0 EndX=-40 EndY=170 EndZ=0
    g16: ArcOfCircle CenterX=-40 CenterY=175 CenterZ=0 NormalX=0 NormalY=0 NormalZ=1 AngleXU=0 Radius=5 StartAngle=3.14159 EndAngle=4.71239
    g17: LineSegment StartX=-45 StartY=175 StartZ=0 EndX=-45 EndY=205 EndZ=0
    g18: GeomPoint [constr] X=-45 Y=210 Z=0
    g19: GeomPoint [constr] X=45 Y=170 Z=0
    g20: ArcOfCircle [constr] CenterX=-40 CenterY=205 CenterZ=0 NormalX=0 NormalY=0 NormalZ=1 AngleXU=0 Radius=17.5 StartAngle=1.5708 EndAngle=3.14159
    g21: LineSegment [constr] StartX=-40 StartY=222.5 StartZ=0 EndX=40 EndY=222.5 EndZ=0
    g22: ArcOfCircle [constr] CenterX=40 CenterY=205 CenterZ=0 NormalX=0 NormalY=0 NormalZ=1 AngleXU=0 Radius=17.5 StartAngle=3.5e-15 EndAngle=1.5708
    g23: LineSegment [constr] StartX=57.5 StartY=205 StartZ=0 EndX=57.5 EndY=175 EndZ=0
    g24: ArcOfCircle [constr] CenterX=40 CenterY=175 CenterZ=0 NormalX=0 NormalY=0 NormalZ=1 AngleXU=0 Radius=17.5 StartAngle=4.71239 EndAngle=6.28319
    g25: LineSegment [constr] StartX=40 StartY=157.5 StartZ=0 EndX=-40 EndY=157.5 EndZ=0
    g26: ArcOfCircle [constr] CenterX=-40 CenterY=175 CenterZ=0 NormalX=0 NormalY=0 NormalZ=1 AngleXU=0 Radius=17.5 StartAngle=3.14159 EndAngle=4.71239
    g27: LineSegment [constr] StartX=-57.5 StartY=175 StartZ=0 EndX=-57.5 EndY=205 EndZ=0
    g28: GeomPoint [constr] X=-57.5 Y=222.5 Z=0
    g29: GeomPoint [constr] X=57.5 Y=157.5 Z=0
    g30: Circle CenterX=-22.5 CenterY=222.5 CenterZ=0 NormalX=0 NormalY=0 NormalZ=1 AngleXU=0 Radius=2
    g31: Circle CenterX=22.5 CenterY=222.5 CenterZ=0 NormalX=0 NormalY=0 NormalZ=1 AngleXU=0 Radius=2
    g32: Circle CenterX=-22.5 CenterY=157.5 CenterZ=0 NormalX=0 NormalY=0 NormalZ=1 AngleXU=0 Radius=2
    g33: Circle CenterX=-57.5 CenterY=190 CenterZ=0 NormalX=0 NormalY=0 NormalZ=1 AngleXU=0 Radius=2
    g34: Circle CenterX=57.5 CenterY=190 CenterZ=0 NormalX=0 NormalY=0 NormalZ=1 AngleXU=0 Radius=2
    g35: Circle CenterX=22.5 CenterY=157.5 CenterZ=0 NormalX=0 NormalY=0 NormalZ=1 AngleXU=0 Radius=2
  constraints (79):
    c: Tangent(g0,g1) = 1.5708
    c: Tangent(g1,g2) = 1.5708
    c: Tangent(g2,g3) = 1.5708
    c: Tangent(g3,g4) = 1.5708
    c: Tangent(g4,g5) = 1.5708
    c: Tangent(g5,g6) = 1.5708
    c: Tangent(g6,g7) = 1.5708
    c: Tangent(g7,g0) = 1.5708
    c: Horizontal(g1)
    c: Horizontal(g5)
    c: Vertical(g3)
    c: Vertical(g7)
    c: Equal(g0,g2)
    c: Equal(g2,g4)
    c: Equal(g4,g6)
    c: PointOnObject(g8,g1)
    c: PointOnObject(g8,g7)
    c: PointOnObject(g9,g3)
    c: PointOnObject(g9,g5)
    c: Coincident(g4,g-8)
    c: Coincident(g0,g-7)
    c: Radius(g0) = 25
    c: Tangent(g10,g11) = 1.5708
    c: Tangent(g11,g12) = 1.5708
    c: Tangent(g12,g13) = 1.5708
    c: Tangent(g13,g14) = 1.5708
    c: Tangent(g14,g15) = 1.5708
    c: Tangent(g15,g16) = 1.5708
    c: Tangent(g16,g17) = 1.5708
    c: Tangent(g17,g10) = 1.5708
    c: Horizontal(g11)
    c: Horizontal(g15)
    c: Vertical(g13)
    c: Vertical(g17)
    c: Equal(g10,g12)
    c: Equal(g12,g14)
    c: Equal(g14,g16)
    c: PointOnObject(g18,g11)
    c: PointOnObject(g18,g17)
    c: PointOnObject(g19,g13)
    c: PointOnObject(g19,g15)
    c: Coincident(g10,g0)
    c: Coincident(g14,g4)
    c: DistanceX(g12,g-6) = 5
    c: Tangent(g20,g21) = 1.5708
    c: Tangent(g21,g22) = 1.5708
    c: Tangent(g22,g23) = 1.5708
    c: Tangent(g23,g24) = 1.5708
    c: Tangent(g24,g25) = 1.5708
    c: Tangent(g25,g26) = 1.5708
    c: Tangent(g26,g27) = 1.5708
    c: Tangent(g27,g20) = 1.5708
    c: Horizontal(g21)
    c: Horizontal(g25)
    c: Vertical(g27)
    c: Equal(g20,g22)
    c: Equal(g22,g24)
    c: Equal(g24,g26)
    c: PointOnObject(g28,g21)
    c: PointOnObject(g28,g27)
    c: PointOnObject(g29,g23)
    c: PointOnObject(g29,g25)
    c: Coincident(g24,g4)
    c: Coincident(g20,g0)
    c: Symmetric(g-8,g3,g23)
    c: PointOnObject(g30,g21)
    c: PointOnObject(g32,g25)
    c: Symmetric(g30,g31,g-2)
    c: Symmetric(g26,g20,g33)
    c: Symmetric(g23,g22,g34)
    c: Symmetric(g35,g32,g-2)
    c: Vertical(g35,g31)
    c: Equal(g30,g31)
    c: Equal(g30,g34)
    c: Equal(g30,g35)
    c: Equal(g30,g32)
    c: Equal(g30,g33)
    c: Diameter(g30) = 4
    c: DistanceX(g30,g31) = 45
FEATURE [PartDesign::Pad] Pad016
  AddSubType = 0
  AlongSketchNormal = false
  AutoTaperInnerAngle = true
  CheckUpToFaceLimits = true
  ClaimChildren = false
  Direction = (1,1e-16,1e-16)
  Fit = 0
  FitJoin = 0
  InnerFit = 0
  InnerFitJoin = 0
  InvalidShape = false
  Length = 5
  Length2 = 100
  Linearize = true
  NewSolid = false
  Profile = -> Sketch039
  Refine = true
  Suppress = false
  TaperInnerAngle = 0
  TaperInnerAngleRev = 0
  TreeRank = 367
  Type = 0
  ValidateShape = true
  _ProfileBasedVersion = 1
FEATURE [Sketcher::SketchObject] Sketch040
  ArcFitTolerance = 1e-06
  AttachmentSupport = -> [Pad016]
  ExternalBSplineMaxDegree = 5
  ExternalBSplineTolerance = 0.0001
  ExternalGeometry = -> [Binder,Pad016]
  FullyConstrained = true
  InternalTolerance = 1e-06
  InvalidShape = false
  MakeInternals = true
  MapMode = 5
  Placement = pos=(175,3.92e-14,0) rot=(0.57735,-0.57735,-0.57735;2.0944rad)
  Support = -> [Pad016]
  TreeRank = 368
  ValidateShape = true
  sketch-geometry (10):
    g0: ArcOfCircle CenterX=-40 CenterY=205 CenterZ=0 NormalX=0 NormalY=0 NormalZ=1 AngleXU=0 Radius=9.5 StartAngle=1.5708 EndAngle=3.14159
    g1: LineSegment StartX=-40 StartY=214.5 StartZ=0 EndX=40 EndY=214.5 EndZ=0
    g2: ArcOfCircle CenterX=40 CenterY=205 CenterZ=0 NormalX=0 NormalY=0 NormalZ=1 AngleXU=0 Radius=9.5 StartAngle=-1.43965e-11 EndAngle=1.5708
    g3: LineSegment StartX=49.5 StartY=205 StartZ=0 EndX=49.5 EndY=175 EndZ=0
    g4: ArcOfCircle CenterX=40 CenterY=175 CenterZ=0 NormalX=0 NormalY=0 NormalZ=1 AngleXU=0 Radius=9.5 StartAngle=4.71239 EndAngle=6.28319
    g5: LineSegment StartX=40 StartY=165.5 StartZ=0 EndX=-40 EndY=165.5 EndZ=0
    g6: ArcOfCircle CenterX=-40 CenterY=175 CenterZ=0 NormalX=0 NormalY=0 NormalZ=1 AngleXU=0 Radius=9.5 StartAngle=3.14159 EndAngle=4.71239
    g7: LineSegment StartX=-49.5 StartY=175 StartZ=0 EndX=-49.5 EndY=205 EndZ=0
    g8: GeomPoint [constr] X=-49.5 Y=214.5 Z=0
    g9: GeomPoint [constr] X=49.5 Y=165.5 Z=0
  constraints (22):
    c: Tangent(g0,g1) = 1.5708
    c: Tangent(g1,g2) = 1.5708
    c: Tangent(g2,g3) = 1.5708
    c: Tangent(g3,g4) = 1.5708
    c: Tangent(g4,g5) = 1.5708
    c: Tangent(g5,g6) = 1.5708
    c: Tangent(g6,g7) = 1.5708
    c: Tangent(g7,g0) = 1.5708
    c: Horizontal(g1)
    c: Horizontal(g5)
    c: Vertical(g3)
    c: Vertical(g7)
    c: Equal(g0,g2)
    c: Equal(g2,g4)
    c: Equal(g4,g6)
    c: PointOnObject(g8,g1)
    c: PointOnObject(g8,g7)
    c: PointOnObject(g9,g3)
    c: PointOnObject(g9,g5)
    c: Coincident(g0,g-3)
    c: Coincident(g4,g-4)
    c: DistanceX(g3,g-4) = 0.5
FEATURE [PartDesign::Pad] Pad017
  AddSubType = 0
  AlongSketchNormal = false
  AutoTaperInnerAngle = true
  BaseFeature = -> Pad016
  CheckUpToFaceLimits = true
  ClaimChildren = false
  Direction = (-1,-1e-16,-1e-16)
  Fit = 0
  FitJoin = 0
  InnerFit = 0
  InnerFitJoin = 0
  InvalidShape = false
  Length = 25
  Length2 = 100
  Linearize = true
  NewSolid = false
  Profile = -> Sketch040
  Refine = true
  Suppress = false
  TaperInnerAngle = 0
  TaperInnerAngleRev = 0
  TreeRank = 369
  Type = 0
  ValidateShape = true
  _ProfileBasedVersion = 1
FEATURE [Sketcher::SketchObject] Sketch041
  ArcFitTolerance = 1e-06
  AttachmentSupport = -> [Pad017]
  ExternalBSplineMaxDegree = 5
  ExternalBSplineTolerance = 0.0001
  ExternalGeometry = -> [Pad017]
  FullyConstrained = true
  InternalTolerance = 1e-06
  InvalidShape = false
  MakeInternals = true
  MapMode = 5
  Placement = pos=(150,0,0) rot=(0.57735,-0.57735,-0.57735;2.0944rad)
  Support = -> [Pad017]
  TreeRank = 370
  ValidateShape = true
FEATURE [PartDesign::Pad] Pad018
  AddSubType = 0
  AlongSketchNormal = false
  AutoTaperInnerAngle = true
  BaseFeature = -> Pad017
  CheckUpToFaceLimits = true
  ClaimChildren = false
  Direction = (-1,0,0)
  Fit = 0
  FitJoin = 0
  InnerFit = 0
  InnerFitJoin = 0
  InvalidShape = false
  Length = 3
  Length2 = 100
  Linearize = true
  NewSolid = false
  Profile = -> Sketch041
  Refine = true
  Suppress = false
  TaperInnerAngle = 0
  TaperInnerAngleRev = 0
  TreeRank = 371
  Type = 0
  ValidateShape = true
  _ProfileBasedVersion = 1
FEATURE [Sketcher::SketchObject] Sketch042
  ArcFitTolerance = 1e-06
  AttachmentSupport = -> [Pad018]
  ExternalBSplineMaxDegree = 5
  ExternalBSplineTolerance = 0.0001
  ExternalGeometry = -> [Pad018]
  FullyConstrained = true
  InternalTolerance = 1e-06
  InvalidShape = false
  MakeInternals = true
  MapMode = 5
  Placement = pos=(180,4.03e-14,0) rot=(0.57735,0.57735,0.57735;2.0944rad)
  Support = -> [Pad018]
  TreeRank = 372
  ValidateShape = true
  sketch-geometry (4):
    g0: LineSegment StartX=-45 StartY=205 StartZ=0 EndX=45 EndY=205 EndZ=0
    g1: LineSegment StartX=45 StartY=205 StartZ=0 EndX=45 EndY=210 EndZ=0
    g2: LineSegment StartX=45 StartY=210 StartZ=0 EndX=-45 EndY=210 EndZ=0
    g3: LineSegment StartX=-45 StartY=210 StartZ=0 EndX=-45 EndY=205 EndZ=0
  constraints (10):
    c: Coincident(g0,g1)
    c: Coincident(g1,g2)
    c: Coincident(g2,g3)
    c: Coincident(g3,g0)
    c: Horizontal(g2)
    c: Vertical(g1)
    c: Vertical(g3)
    c: Coincident(g0,g-3)
    c: Coincident(g0,g-4)
    c: PointOnObject(g-4,g2)
FEATURE [PartDesign::Pad] Pad019
  AddSubType = 0
  AlongSketchNormal = false
  AutoTaperInnerAngle = true
  BaseFeature = -> Pad018
  CheckUpToFaceLimits = true
  ClaimChildren = false
  Direction = (1,1e-16,1e-16)
  Fit = 0
  FitJoin = 0
  InnerFit = 0
  InnerFitJoin = 0
  InvalidShape = false
  Length = 30
  Length2 = 100
  Linearize = true
  NewSolid = false
  Profile = -> Sketch042
  Refine = true
  Reversed = true
  Suppress = false
  TaperInnerAngle = 0
  TaperInnerAngleRev = 0
  TreeRank = 373
  Type = 0
  ValidateShape = true
  _ProfileBasedVersion = 1
FEATURE [PartDesign::Draft] Draft002
  AddSubType = 0
  Angle = 12
  Base = -> Pad019 [Face32]
  BaseFeature = -> Pad019
  InvalidShape = false
  NeutralPlane = -> Pad019 [Face25]
  NewSolid = false
  Refine = true
  Reversed = true
  SupportTransform = false
  Suppress = false
  TreeRank = 374
  ValidateShape = true
FEATURE [PartDesign::Fillet] Fillet016
  AddSubType = 0
  Base = -> Draft002 [Edge75,Edge82]
  BaseFeature = -> Draft002
  InvalidShape = false
  NewSolid = false
  Radius = 4
  Refine = true
  SupportTransform = false
  Suppress = false
  TreeRank = 375
  UseAllEdges = false
  ValidateShape = true
FEATURE [PartDesign::Fillet] Fillet017
  AddSubType = 0
  Base = -> Fillet016 [Edge4]
  BaseFeature = -> Fillet016
  InvalidShape = false
  NewSolid = false
  Radius = 5
  Refine = true
  SupportTransform = false
  Suppress = false
  TreeRank = 376
  UseAllEdges = false
  ValidateShape = true
FEATURE [PartDesign::Chamfer] Chamfer028
  AddSubType = 0
  Angle = 45
  Base = -> Fillet017 [Edge18]
  BaseFeature = -> Fillet017
  ChamferType = 0
  FlipDirection = false
  InvalidShape = false
  NewSolid = false
  Refine = true
  Size = 1
  Size2 = 1
  SupportTransform = false
  Suppress = false
  TreeRank = 377
  UseAllEdges = false
  ValidateShape = true
FEATURE [PartDesign::Chamfer] Chamfer029
  AddSubType = 0
  Angle = 45
  Base = -> Chamfer028 [Edge114,Edge110,Edge74]
  BaseFeature = -> Chamfer028
  ChamferType = 0
  FlipDirection = false
  InvalidShape = false
  NewSolid = false
  Refine = true
  Size = 1
  Size2 = 1
  SupportTransform = false
  Suppress = false
  TreeRank = 378
  UseAllEdges = false
  ValidateShape = true
FEATURE [PartDesign::Fillet] Fillet018
  AddSubType = 0
  Base = -> Chamfer029 [Edge146]
  BaseFeature = -> Chamfer029
  InvalidShape = false
  NewSolid = false
  Radius = 2
  Refine = true
  SupportTransform = false
  Suppress = false
  TreeRank = 379
  UseAllEdges = false
  ValidateShape = true
FEATURE [App::Link] Link002  label="HandleLeft"
  AutoLinkLabel = true
  AutoPlacement = true
  LinkPlacement = pos=(0,0,0) rot=(0,0,1;3.14159rad)
  LinkedObject = -> Body014
  Placement = pos=(0,0,0) rot=(0,0,1;3.14159rad)
  SyncGroupVisibility = false
  TreeRank = 380
  _LinkVersion = 1
FEATURE [TechDraw::DrawViewDimension] Dimension001
  AngleOverride = false
  Arbitrary = false
  ArbitraryTolerances = false
  EqualTolerance = true
  ExtensionAngle = 0
  FormatSpec = %.2f
  FormatSpecOverTolerance = %+.2f
  FormatSpecUnderTolerance = %+.2f
  Inverted = false
  LineAngle = 0
  LockPosition = false
  MeasureType = 1
  OverTolerance = 0
  References2D = -> [ProjItem002]
  Rotation = 0
  ScaleType = 0
  TheoreticalExact = false
  TreeRank = 381
  Type = 2
  UnderTolerance = 0
  X = -90
  Y = 3.09696e-09
FEATURE [TechDraw::DrawViewDimension] Dimension002
  AngleOverride = false
  Arbitrary = false
  ArbitraryTolerances = false
  EqualTolerance = true
  ExtensionAngle = 0
  FormatSpec = %.2f
  FormatSpecOverTolerance = %+.2f
  FormatSpecUnderTolerance = %+.2f
  Inverted = false
  LineAngle = 0
  LockPosition = false
  MeasureType = 1
  OverTolerance = 0
  References2D = -> [ProjItem002]
  Rotation = 0
  ScaleType = 0
  TheoreticalExact = false
  TreeRank = 382
  Type = 1
  UnderTolerance = 0
  X = -2.53293e-09
  Y = 30
FEATURE [TechDraw::DrawPage] Page001  label="Laser10mm-Bottom"
  KeepUpdated = true
  NextBalloonIndex = 1
  ProjectionType = 0
  Template = -> Template001
  TreeRank = 300
  Views = -> [ProjGroup002,Dimension001,Dimension002]
FEATURE [PartDesign::Chamfer] Chamfer030
  AddSubType = 0
  Angle = 45
  Base = -> Fillet018 [Edge51,Edge53,Edge52,Edge49,Edge48,Edge50]
  BaseFeature = -> Fillet018
  ChamferType = 0
  FlipDirection = false
  InvalidShape = false
  NewSolid = false
  Refine = true
  Size = 3
  Size2 = 1
  SupportTransform = false
  Suppress = false
  TreeRank = 393
  UseAllEdges = false
  ValidateShape = true
FEATURE [PartDesign::Body] Body014  label="HandleRight"
  AutoGroupSolids = false
  ClaimAllChildren = false
  ExportMode = 0
  Group = -> [Binder,Sketch039,Pad016,Sketch040,Pad017,Sketch041,Pad018,Sketch042,Pad019,Draft002,Fillet016,Fillet017,Chamfer028,Chamfer029,Fillet018,Chamfer030]
  InvalidShape = false
  Origin = -> Origin017
  SingleSolid = true
  Tip = -> Chamfer030
  TreeRank = 364
  ValidateShape = true
  _ExportChildren = -> [Binder,Pad016,Pad017,Pad018,Pad019,Draft002,Fillet016,Fillet017,Chamfer028,Chamfer029,Fillet018,Chamfer030]
  _GroupVersion = 1
FEATURE [Sketcher::SketchObject] Sketch043
  ArcFitTolerance = 1e-06
  AttachmentSupport = -> [XY_Plane014]
  ExternalBSplineMaxDegree = 5
  ExternalBSplineTolerance = 0.0001
  ExternalGeometry = -> [Fillet014]
  FullyConstrained = true
  InternalTolerance = 1e-06
  InvalidShape = false
  MakeInternals = true
  MapMode = 5
  Support = -> [XY_Plane014]
  TreeRank = 394
  ValidateShape = true
  sketch-geometry (4):
    g0: LineSegment StartX=-0.25 StartY=115 StartZ=0 EndX=0.25 EndY=115 EndZ=0
    g1: LineSegment StartX=0.25 StartY=115 StartZ=0 EndX=0.25 EndY=-130 EndZ=0
    g2: LineSegment StartX=0.25 StartY=-130 StartZ=0 EndX=-0.25 EndY=-130 EndZ=0
    g3: LineSegment StartX=-0.25 StartY=-130 StartZ=0 EndX=-0.25 EndY=115 EndZ=0
  constraints (11):
    c: Coincident(g0,g1)
    c: Coincident(g1,g2)
    c: Coincident(g2,g3)
    c: Coincident(g3,g0)
    c: Horizontal(g2)
    c: Vertical(g1)
    c: Vertical(g3)
    c: Symmetric(g0,g0,g-2)
    c: PointOnObject(g0,g-3)
    c: PointOnObject(g1,g-4)
    c: DistanceX(g0,g0) = 0.5
FEATURE [PartDesign::Pocket] Pocket023
  AddSubType = 1
  AutoTaperInnerAngle = true
  BaseFeature = -> Fillet014
  CheckUpToFaceLimits = true
  ClaimChildren = false
  Direction = (0,0,-1)
  Fit = 0
  FitJoin = 0
  InnerFit = 0
  InnerFitJoin = 0
  InvalidShape = false
  Length = 5
  Length2 = 100
  Linearize = true
  NewSolid = false
  Profile = -> Sketch043
  Refine = true
  Reversed = true
  Suppress = false
  TaperInnerAngle = 0
  TaperInnerAngleRev = 0
  TreeRank = 395
  Type = 1
  ValidateShape = true
  _ProfileBasedVersion = 1
  _Version = 1
FEATURE [PartDesign::Chamfer] Chamfer031
  AddSubType = 0
  Angle = 45
  Base = -> Pocket023 [Edge35,Edge21,Edge33,Edge22]
  BaseFeature = -> Pocket023
  ChamferType = 0
  FlipDirection = false
  InvalidShape = false
  NewSolid = false
  Refine = true
  Size = 2
  Size2 = 1
  SupportTransform = false
  Suppress = false
  TreeRank = 396
  UseAllEdges = false
  ValidateShape = true
FEATURE [App::DocumentObjectGroup] Group005  label="Hinges"
  ClaimAllChildren = true
  ExportMode = 1
  Group = -> [Screw003,Screw002,Screw001,Screw,Link001,Link,Part]
  TreeRank = 397
  _GroupVersion = 1
FEATURE [Sketcher::SketchObject] Sketch044
  ArcFitTolerance = 1e-06
  AttachmentSupport = -> [XY_Plane014]
  ExternalBSplineMaxDegree = 5
  ExternalBSplineTolerance = 0.0001
  FullyConstrained = true
  InternalTolerance = 1e-06
  InvalidShape = false
  MakeInternals = true
  MapMode = 5
  Support = -> [XY_Plane014]
  TreeRank = 398
  ValidateShape = true
  sketch-geometry (9):
    g0: LineSegment [constr] StartX=-10 StartY=60 StartZ=0 EndX=-10 EndY=100 EndZ=0
    g1: LineSegment [constr] StartX=-10 StartY=100 StartZ=0 EndX=10 EndY=100 EndZ=0
    g2: LineSegment [constr] StartX=10 StartY=100 StartZ=0 EndX=10 EndY=60 EndZ=0
    g3: LineSegment [constr] StartX=10 StartY=60 StartZ=0 EndX=-10 EndY=60 EndZ=0
    g4: GeomPoint [constr] X=-2.459e-12 Y=80 Z=0
    g5: Circle CenterX=-10 CenterY=100 CenterZ=0 NormalX=0 NormalY=0 NormalZ=1 AngleXU=0 Radius=1.6
    g6: Circle CenterX=10 CenterY=100 CenterZ=0 NormalX=0 NormalY=0 NormalZ=1 AngleXU=0 Radius=1.6
    g7: Circle CenterX=10 CenterY=60 CenterZ=0 NormalX=0 NormalY=0 NormalZ=1 AngleXU=0 Radius=1.6
    g8: Circle CenterX=-10 CenterY=60 CenterZ=0 NormalX=0 NormalY=0 NormalZ=1 AngleXU=0 Radius=1.6
  constraints (21):
    c: Coincident(g0,g1)
    c: Coincident(g1,g2)
    c: Coincident(g2,g3)
    c: Coincident(g3,g0)
    c: Horizontal(g1)
    c: Horizontal(g3)
    c: Vertical(g0)
    c: Vertical(g2)
    c: Symmetric(g1,g0,g4)
    c: PointOnObject(g4,g-2)
    c: Coincident(g5,g0)
    c: Coincident(g6,g1)
    c: Coincident(g7,g2)
    c: Coincident(g8,g0)
    c: Equal(g8,g7)
    c: Equal(g8,g6)
    c: Equal(g8,g5)
    c: Diameter(g8) = 3.2
    c: DistanceX(g1,g1) = 20
    c: DistanceY(g2,g2) = 40
    c: DistanceY(g-1,g4) = 80
FEATURE [PartDesign::Pocket] Pocket024
  AddSubType = 1
  AutoTaperInnerAngle = true
  BaseFeature = -> Chamfer031
  CheckUpToFaceLimits = true
  ClaimChildren = false
  Direction = (0,0,-1)
  Fit = 0
  FitJoin = 0
  InnerFit = 0
  InnerFitJoin = 0
  InvalidShape = false
  Length = 5
  Length2 = 100
  Linearize = true
  NewSolid = false
  Profile = -> Sketch044
  Refine = true
  Reversed = true
  Suppress = false
  TaperInnerAngle = 0
  TaperInnerAngleRev = 0
  TreeRank = 399
  Type = 1
  ValidateShape = true
  _ProfileBasedVersion = 1
  _Version = 1
FEATURE [PartDesign::Mirrored] Mirrored003
  AddSubType = 0
  BaseFeature = -> Pocket024
  CopyShape = false
  InvalidShape = false
  MirrorPlane = -> XZ_Plane014
  NewSolid = false
  OriginalSubs = -> [Pocket024]
  Originals = -> [Pocket024]
  ParallelTransform = true
  Refine = true
  SubTransform = true
  Suppress = false
  TreeRank = 400
  ValidateShape = true
  _Version = 3
FEATURE [PartDesign::Body] Body013  label="Door"
  AutoGroupSolids = false
  ClaimAllChildren = false
  ExportMode = 0
  Group = -> [Sketch035,Pad015,Sketch036,Import005,Import006,Pocket020,Fillet014,Sketch043,Pocket023,Chamfer031,Sketch044,Pocket024,Mirrored003]
  InvalidShape = false
  Origin = -> Origin016
  Placement = pos=(0,0,230) rot=(0,0,1;0rad)
  Tip = -> Mirrored003
  TreeRank = 332
  ValidateShape = true
  _ExportChildren = -> [Pad015,Import005,Import006,Pocket020,Fillet014,Pocket023,Chamfer031,Pocket024,Mirrored003]
  _GroupVersion = 1
FEATURE [Sketcher::SketchObject] Sketch045
  ArcFitTolerance = 1e-06
  AttachmentSupport = -> [XY_Plane016]
  ExternalBSplineMaxDegree = 5
  ExternalBSplineTolerance = 0.0001
  FullyConstrained = true
  InternalTolerance = 1e-06
  InvalidShape = false
  MakeInternals = true
  MapMode = 5
  Support = -> [XY_Plane016]
  TreeRank = 411
  ValidateShape = true
  sketch-geometry (14):
    g0: LineSegment [constr] StartX=-10 StartY=-20 StartZ=0 EndX=-10 EndY=20 EndZ=0
    g1: LineSegment [constr] StartX=-10 StartY=20 StartZ=0 EndX=10 EndY=20 EndZ=0
    g2: LineSegment [constr] StartX=10 StartY=20 StartZ=0 EndX=10 EndY=-20 EndZ=0
    g3: LineSegment [constr] StartX=10 StartY=-20 StartZ=0 EndX=-10 EndY=-20 EndZ=0
    g4: GeomPoint [constr] X=0 Y=0 Z=0
    g5: Circle CenterX=-10 CenterY=20 CenterZ=0 NormalX=0 NormalY=0 NormalZ=1 AngleXU=0 Radius=2
    g6: Circle CenterX=10 CenterY=20 CenterZ=0 NormalX=0 NormalY=0 NormalZ=1 AngleXU=0 Radius=2
    g7: Circle CenterX=10 CenterY=-20 CenterZ=0 NormalX=0 NormalY=0 NormalZ=1 AngleXU=0 Radius=2
    g8: Circle CenterX=-10 CenterY=-20 CenterZ=0 NormalX=0 NormalY=0 NormalZ=1 AngleXU=0 Radius=2
    g9: LineSegment StartX=-15 StartY=-25 StartZ=0 EndX=-15 EndY=25 EndZ=0
    g10: LineSegment StartX=-15 StartY=25 StartZ=0 EndX=15 EndY=25 EndZ=0
    g11: LineSegment StartX=15 StartY=25 StartZ=0 EndX=15 EndY=-25 EndZ=0
    g12: LineSegment StartX=15 StartY=-25 StartZ=0 EndX=-15 EndY=-25 EndZ=0
    g13: GeomPoint [constr] X=0 Y=0 Z=0
  constraints (32):
    c: Coincident(g0,g1)
    c: Coincident(g1,g2)
    c: Coincident(g2,g3)
    c: Coincident(g3,g0)
    c: Horizontal(g1)
    c: Horizontal(g3)
    c: Vertical(g0)
    c: Vertical(g2)
    c: Symmetric(g1,g0,g4)
    c: Coincident(g4,g-1)
    c: DistanceX(g1,g1) = 20
    c: DistanceY(g2,g2) = 40
    c: Coincident(g5,g0)
    c: Coincident(g6,g1)
    c: Coincident(g7,g2)
    c: Coincident(g8,g0)
    c: Equal(g7,g8)
    c: Equal(g7,g5)
    c: Equal(g7,g6)
    c: Diameter(g7) = 4
    c: Coincident(g9,g10)
    c: Coincident(g10,g11)
    c: Coincident(g11,g12)
    c: Coincident(g12,g9)
    c: Horizontal(g10)
    c: Horizontal(g12)
    c: Vertical(g9)
    c: Vertical(g11)
    c: Symmetric(g10,g9,g13)
    c: Coincident(g13,g4)
    c: DistanceX(g10,g10) = 30
    c: DistanceY(g11,g11) = 50
FEATURE [PartDesign::Pad] Pad020
  AddSubType = 0
  AlongSketchNormal = false
  AutoTaperInnerAngle = true
  CheckUpToFaceLimits = true
  ClaimChildren = false
  Direction = (0,0,1)
  Fit = 0
  FitJoin = 0
  InnerFit = 0
  InnerFitJoin = 0
  InvalidShape = false
  Length = 7
  Length2 = 100
  Linearize = true
  NewSolid = false
  Profile = -> Sketch045
  Refine = true
  Reversed = true
  Suppress = false
  TaperInnerAngle = 0
  TaperInnerAngleRev = 0
  TreeRank = 412
  Type = 0
  ValidateShape = true
  _ProfileBasedVersion = 1
FEATURE [PartDesign::Fillet] Fillet019
  AddSubType = 0
  Base = -> Pad020 [Edge8,Edge1,Edge2,Edge5]
  BaseFeature = -> Pad020
  InvalidShape = false
  NewSolid = false
  Radius = 5
  Refine = true
  SupportTransform = false
  Suppress = false
  TreeRank = 413
  UseAllEdges = false
  ValidateShape = true
FEATURE [PartDesign::Chamfer] Chamfer032
  AddSubType = 0
  Angle = 45
  Base = -> Fillet019 [Face2,Face5]
  BaseFeature = -> Fillet019
  ChamferType = 0
  FlipDirection = false
  InvalidShape = false
  NewSolid = false
  Refine = true
  Size = 1
  Size2 = 1
  SupportTransform = false
  Suppress = false
  TreeRank = 414
  UseAllEdges = false
  ValidateShape = true
FEATURE [PartDesign::Body] Body015  label="DoorLinkerRear"
  AutoGroupSolids = false
  ClaimAllChildren = false
  ExportMode = 0
  Group = -> [Sketch045,Pad020,Fillet019,Chamfer032]
  InvalidShape = false
  Origin = -> Origin018
  Placement = pos=(0,80,230) rot=(0,0,1;0rad)
  SingleSolid = true
  Tip = -> Chamfer032
  TreeRank = 410
  ValidateShape = true
  _ExportChildren = -> [Pad020,Fillet019,Chamfer032]
  _GroupVersion = 1
FEATURE [App::Link] Link009  label="DoorLinkerFront"
  AutoLinkLabel = true
  AutoPlacement = true
  LinkPlacement = pos=(0,-160,0) rot=(0,0,1;0rad)
  LinkTransform = true
  LinkedObject = -> Body015
  Placement = pos=(0,-160,0) rot=(0,0,1;0rad)
  SyncGroupVisibility = false
  TreeRank = 415
  _LinkVersion = 1
FEATURE [App::DocumentObjectGroup] Group003  label="DoorAssembly"
  ClaimAllChildren = true
  ExportMode = 1
  Group = -> [Body013,Group005,Body015,Link009]
  TreeRank = 321
  _GroupVersion = 1
FEATURE [TechDraw::DrawSVGTemplate] Template004
  Height = 210
  Orientation = 1
  TreeRank = 417
  Width = 297
FEATURE [TechDraw::DrawSVGTemplate] Template005
  Height = 210
  Orientation = 1
  TreeRank = 459
  Width = 297
FEATURE [TechDraw::DrawProjGroupItem] ProjItem006  label="Front007"
  CoarseView = false
  Direction = (0,0,1)
  Focus = 100
  HardHidden = false
  IsoCount = 0
  IsoHidden = false
  IsoVisible = false
  LockPosition = true
  Perspective = false
  Rotation = 0
  RotationVector = (-1,0,0)
  ScaleType = 2
  ScrubCount = 0
  SeamHidden = false
  SeamVisible = true
  SmoothHidden = false
  SmoothVisible = true
  TreeRank = 462
  Type = 0
  X = 0
  XDirection = (-1,0,0)
  Y = 0
FEATURE [TechDraw::DrawProjGroup] ProjGroup006
  Anchor = -> ProjItem006
  AutoDistribute = true
  LockPosition = false
  ProjectionType = 0
  Rotation = 0
  ScaleType = 0
  TreeRank = 463
  Views = -> [ProjItem006]
  X = 131.483
  Y = 118.551
  spacingX = 15
  spacingY = 15
FEATURE [TechDraw::DrawPage] Page005  label="Laser5mmTopBasket"
  KeepUpdated = true
  NextBalloonIndex = 1
  ProjectionType = 0
  Template = -> Template005
  TreeRank = 460
  Views = -> [ProjGroup006]
FEATURE [TechDraw::DrawSVGTemplate] Template006
  Height = 210
  Orientation = 1
  TreeRank = 465
  Width = 297
FEATURE [TechDraw::DrawProjGroupItem] ProjItem007  label="Front008"
  CoarseView = false
  Direction = (0,0,-1)
  Focus = 100
  HardHidden = false
  IsoCount = 0
  IsoHidden = false
  IsoVisible = false
  LockPosition = true
  Perspective = false
  Rotation = 0
  RotationVector = (1,0,0)
  ScaleType = 2
  ScrubCount = 0
  SeamHidden = false
  SeamVisible = true
  SmoothHidden = false
  SmoothVisible = true
  TreeRank = 468
  Type = 0
  X = 0
  XDirection = (1,0,0)
  Y = 0
FEATURE [TechDraw::DrawProjGroup] ProjGroup007
  Anchor = -> ProjItem007
  AutoDistribute = true
  LockPosition = false
  ProjectionType = 0
  Rotation = 0
  ScaleType = 0
  TreeRank = 469
  Views = -> [ProjItem007]
  X = 12.3647
  Y = 117.29
  spacingX = 15
  spacingY = 15
FEATURE [TechDraw::DrawPage] Page006  label="Laser5mmEquerres"
  KeepUpdated = true
  NextBalloonIndex = 1
  ProjectionType = 0
  Template = -> Template006
  TreeRank = 466
  Views = -> [ProjGroup007]
FEATURE [App::DocumentObjectGroup] Group006  label="Handles"
  ClaimAllChildren = true
  ExportMode = 1
  Group = -> [Body014,Link002]
  TreeRank = 470
  _GroupVersion = 1
FEATURE [App::Link] Link015  label="CrateTop"
  AutoLinkLabel = true
  AutoPlacement = true
  LinkPlacement = pos=(0,-2.6226e-05,220) rot=(0,0,1;0rad)
  LinkedObject = -> Part001
  Placement = pos=(0,-2.6226e-05,220) rot=(0,0,1;0rad)
  SyncGroupVisibility = false
  TreeRank = 502
  _LinkVersion = 1
FEATURE [Sketcher::SketchObject] Sketch052
  ArcFitTolerance = 1e-06
  AttachmentSupport = -> [XZ_Plane013]
  ExternalBSplineMaxDegree = 5
  ExternalBSplineTolerance = 0.0001
  ExternalGeometry = -> [Pad014]
  FixShape = 1
  FullyConstrained = true
  InternalTolerance = 1e-06
  InvalidShape = false
  MakeInternals = false
  MapMode = 5
  Placement = pos=(0,0,0) rot=(1,0,0;1.5708rad)
  Support = -> [XZ_Plane013]
  TreeRank = 503
  ValidateShape = false
  sketch-geometry (4):
    g0: LineSegment StartX=-165 StartY=11 StartZ=0 EndX=165 EndY=11 EndZ=0
    g1: LineSegment StartX=165 StartY=11 StartZ=0 EndX=165 EndY=21 EndZ=0
    g2: LineSegment StartX=165 StartY=21 StartZ=0 EndX=-165 EndY=21 EndZ=0
    g3: LineSegment StartX=-165 StartY=21 StartZ=0 EndX=-165 EndY=11 EndZ=0
  constraints (10):
    c: Coincident(g0,g1)
    c: Coincident(g1,g2)
    c: Coincident(g2,g3)
    c: Coincident(g3,g0)
    c: Horizontal(g2)
    c: Vertical(g1)
    c: Vertical(g3)
    c: Coincident(g0,g-3)
    c: Coincident(g0,g-4)
    c: DistanceY(g1,g1) = 10
FEATURE [PartDesign::Pocket] Pocket027
  AddSubType = 1
  AlongSketchNormal = false
  AutoTaperInnerAngle = true
  BaseFeature = -> Pad014
  CheckUpToFaceLimits = true
  ClaimChildren = false
  Direction = (0,1,2e-16)
  Fit = 0
  FitJoin = 0
  FixShape = 1
  InnerFit = 0
  InnerFitJoin = 0
  InvalidShape = false
  Length = 5
  Length2 = 10
  Linearize = true
  NewSolid = false
  Profile = -> Sketch052
  ReferenceAxis = -> Sketch052 [N_Axis]
  Refine = true
  Reversed = true
  Suppress = false
  TaperInnerAngle = 0
  TaperInnerAngleRev = 0
  TreeRank = 504
  Type = 1
  ValidateShape = true
  _ProfileBasedVersion = 1
  _Version = 1
FEATURE [PartDesign::Fillet] Fillet013
  AddSubType = 0
  Base = -> Pocket027 [Edge53,Edge30,Edge61,Edge60]
  BaseFeature = -> Pocket027
  InvalidShape = false
  NewSolid = false
  Radius = 10
  Refine = true
  SupportTransform = false
  Suppress = false
  TreeRank = 319
  UseAllEdges = false
  ValidateShape = true
FEATURE [Sketcher::SketchObject] Sketch037
  ArcFitTolerance = 1e-06
  AttachmentSupport = -> [XZ_Plane013]
  ExternalBSplineMaxDegree = 5
  ExternalBSplineTolerance = 0.0001
  ExternalGeometry = -> [Fillet013]
  FullyConstrained = true
  InternalTolerance = 1e-06
  InvalidShape = false
  MakeInternals = true
  MapMode = 5
  Placement = pos=(0,0,0) rot=(1,0,0;1.5708rad)
  Support = -> [XZ_Plane013]
  TreeRank = 350
  ValidateShape = true
  sketch-geometry (4):
    g0: LineSegment StartX=-40.9007 StartY=205 StartZ=0 EndX=-50 EndY=230 EndZ=0
    g1: LineSegment StartX=-50 StartY=230 StartZ=0 EndX=50 EndY=230 EndZ=0
    g2: LineSegment StartX=50 StartY=230 StartZ=0 EndX=40.9007 EndY=205 EndZ=0
    g3: LineSegment StartX=40.9007 StartY=205 StartZ=0 EndX=-40.9007 EndY=205 EndZ=0
  constraints (10):
    c: Coincident(g0,g1)
    c: Coincident(g1,g2)
    c: Coincident(g2,g3)
    c: Coincident(g3,g0)
    c: PointOnObject(g1,g-3)
    c: DistanceY(g2,g2) = 25
    c: DistanceX(g1,g1) = 100
    c: Symmetric(g0,g1,g-2)
    c: Symmetric(g2,g0,g-2)
    c: Angle(g0,g1) = 1.22173
FEATURE [PartDesign::Pocket] Pocket021
  AddSubType = 1
  AutoTaperInnerAngle = true
  BaseFeature = -> Fillet013
  CheckUpToFaceLimits = true
  ClaimChildren = false
  Direction = (0,1,2e-16)
  Fit = 0
  FitJoin = 0
  InnerFit = 0
  InnerFitJoin = 0
  InvalidShape = false
  Length = 5
  Length2 = 100
  Linearize = true
  NewSolid = false
  Profile = -> Sketch037
  Refine = true
  Reversed = true
  Suppress = false
  TaperInnerAngle = 0
  TaperInnerAngleRev = 0
  TreeRank = 351
  Type = 1
  ValidateShape = true
  _ProfileBasedVersion = 1
  _Version = 1
FEATURE [PartDesign::Fillet] Fillet015
  AddSubType = 0
  Base = -> Pocket021 [Edge36,Edge38,Edge40,Edge42]
  BaseFeature = -> Pocket021
  InvalidShape = false
  NewSolid = false
  Radius = 10
  Refine = true
  SupportTransform = false
  Suppress = false
  TreeRank = 352
  UseAllEdges = false
  ValidateShape = true
FEATURE [PartDesign::Body] Body012  label="FrontPart"
  AutoGroupSolids = false
  BaseFeature = -> Chamfer027
  ClaimAllChildren = false
  ExportMode = 0
  Group = -> [Clone001,Sketch032,Pocket018,Sketch033,Pad014,Sketch052,Pocket027,Fillet013,Sketch037,Pocket021,Fillet015]
  InvalidShape = false
  Origin = -> Origin015
  Placement = pos=(0,-120,0) rot=(0,0,1;0rad)
  SingleSolid = true
  Tip = -> Fillet015
  TreeRank = 279
  ValidateShape = true
  _ExportChildren = -> [Clone001,Pocket018,Pad014,Pocket027,Fillet013,Pocket021,Fillet015]
  _GroupVersion = 1
FEATURE [PartDesign::LinearPattern] LinearPattern
  AddSubType = 0
  BaseFeature = -> Pocket022
  CopyShape = false
  Direction = -> Sketch038 [V_Axis]
  FixShape = 1
  InvalidShape = false
  Length = 100
  NewSolid = false
  Occurrences = 2
  OriginalSubs = -> [Pocket022]
  Originals = -> [Pocket022]
  ParallelTransform = true
  Refine = true
  Reversed = true
  SubTransform = true
  Suppress = false
  TreeRank = 505
  ValidateShape = true
  _Version = 3
FEATURE [PartDesign::Body] Body008  label="RightPart"
  AutoGroupSolids = false
  ClaimAllChildren = false
  ExportMode = 0
  Group = -> [Sketch022,Import001,Pad009,Sketch025,Pocket013,Sketch029,Import002,Pocket016,Sketch034,Pocket019,Fillet012,Import004,Sketch038,Pocket022,LinearPattern]
  InvalidShape = false
  Origin = -> Origin011
  Placement = pos=(165,0,0) rot=(0,0,1;0rad)
  SingleSolid = true
  Tip = -> LinearPattern
  TreeRank = 210
  ValidateShape = true
  _ExportChildren = -> [Import001,Pad009,Pocket013,Import002,Pocket016,Pocket019,Fillet012,Import004,Pocket022,LinearPattern]
  _GroupVersion = 1
FEATURE [PartDesign::FeatureBase] Clone
  BaseFeature = -> Body008
  InvalidShape = false
  NewSolid = false
  Placement = pos=(165,0,0) rot=(0,0,1;0rad)
  Suppress = false
  TreeRank = 223
  ValidateShape = true
FEATURE [PartDesign::Body] Body009  label="LeftPart"
  AutoGroupSolids = false
  BaseFeature = -> Body008
  ClaimAllChildren = false
  ExportMode = 0
  Group = -> [Clone]
  InvalidShape = false
  Origin = -> Origin012
  Placement = pos=(-340,0,0) rot=(0,0,1;0rad)
  SingleSolid = true
  Tip = -> Clone
  TreeRank = 224
  ValidateShape = true
  _ExportChildren = -> [Clone]
  _GroupVersion = 1
FEATURE [Sketcher::SketchObject] Sketch053
  ArcFitTolerance = 1e-06
  AttachmentSupport = -> [XZ_Plane012]
  ExternalBSplineMaxDegree = 5
  ExternalBSplineTolerance = 0.0001
  ExternalGeometry = -> [Fillet010]
  FixShape = 1
  FullyConstrained = true
  InternalTolerance = 1e-06
  InvalidShape = false
  MakeInternals = false
  MapMode = 5
  Placement = pos=(0,0,0) rot=(1,0,0;1.5708rad)
  Support = -> [XZ_Plane012]
  TreeRank = 506
  ValidateShape = false
  sketch-geometry (10):
    g0: ArcOfCircle CenterX=111 CenterY=105 CenterZ=0 NormalX=0 NormalY=0 NormalZ=1 AngleXU=0 Radius=10 StartAngle=-1.8e-15 EndAngle=1.5708
    g1: LineSegment StartX=121 StartY=105 StartZ=0 EndX=121 EndY=75 EndZ=0
    g2: ArcOfCircle CenterX=111 CenterY=75 CenterZ=0 NormalX=0 NormalY=0 NormalZ=1 AngleXU=0 Radius=10 StartAngle=4.71239 EndAngle=6.28319
    g3: LineSegment StartX=111 StartY=65 StartZ=0 EndX=31 EndY=65 EndZ=0
    g4: ArcOfCircle CenterX=31 CenterY=75 CenterZ=0 NormalX=0 NormalY=0 NormalZ=1 AngleXU=0 Radius=10 StartAngle=3.14159 EndAngle=4.71239
    g5: LineSegment StartX=21 StartY=75 StartZ=0 EndX=21 EndY=105 EndZ=0
    g6: ArcOfCircle CenterX=31 CenterY=105 CenterZ=0 NormalX=0 NormalY=0 NormalZ=1 AngleXU=0 Radius=10 StartAngle=1.5708 EndAngle=3.14159
    g7: LineSegment StartX=31 StartY=115 StartZ=0 EndX=111 EndY=115 EndZ=0
    g8: GeomPoint [constr] X=121 Y=115 Z=0
    g9: GeomPoint [constr] X=21 Y=65 Z=0
  constraints (24):
    c: Tangent(g0,g1) = 1.5708
    c: Tangent(g1,g2) = 1.5708
    c: Tangent(g2,g3) = 1.5708
    c: Tangent(g3,g4) = 1.5708
    c: Tangent(g4,g5) = 1.5708
    c: Tangent(g5,g6) = 1.5708
    c: Tangent(g6,g7) = 1.5708
    c: Tangent(g7,g0) = 1.5708
    c: Horizontal(g3)
    c: Horizontal(g7)
    c: Vertical(g1)
    c: Vertical(g5)
    c: Equal(g0,g2)
    c: Equal(g2,g4)
    c: Equal(g4,g6)
    c: PointOnObject(g8,g1)
    c: PointOnObject(g8,g7)
    c: PointOnObject(g9,g3)
    c: PointOnObject(g9,g5)
    c: Radius(g6) = 10
    c: DistanceX(g5,g0) = 100
    c: DistanceY(g3,g6) = 50
    c: DistanceY(g-3,g0) = 95
    c: DistanceX(g-1,g5) = 21
FEATURE [PartDesign::Pocket] Pocket028
  AddSubType = 1
  AlongSketchNormal = false
  AutoTaperInnerAngle = true
  BaseFeature = -> Fillet010
  CheckUpToFaceLimits = true
  ClaimChildren = false
  Direction = (0,1,2e-16)
  Fit = 0
  FitJoin = 0
  FixShape = 1
  InnerFit = 0
  InnerFitJoin = 0
  InvalidShape = false
  Length = 5
  Length2 = 10
  Linearize = true
  NewSolid = false
  Profile = -> Sketch053
  ReferenceAxis = -> Sketch053 [N_Axis]
  Refine = true
  Reversed = true
  Suppress = false
  TaperInnerAngle = 0
  TaperInnerAngleRev = 0
  TreeRank = 507
  Type = 1
  ValidateShape = true
  _ProfileBasedVersion = 1
  _Version = 1
FEATURE [PartDesign::Mirrored] Mirrored005
  AddSubType = 0
  BaseFeature = -> Pocket028
  CopyShape = false
  FixShape = 1
  InvalidShape = false
  MirrorPlane = -> Sketch053 [V_Axis]
  NewSolid = false
  OriginalSubs = -> [Pocket028]
  Originals = -> [Pocket028]
  ParallelTransform = true
  Refine = true
  SubTransform = true
  Suppress = false
  TreeRank = 508
  ValidateShape = true
  _Version = 3
FEATURE [PartDesign::Body] Body011  label="RearPart"
  AutoGroupSolids = false
  ClaimAllChildren = false
  ExportMode = 0
  Group = -> [Sketch024,Pad011,Sketch026,Pocket014,Sketch030,Import003,Pocket017,Sketch031,Pad013,Chamfer027,Fillet010,Sketch053,Pocket028,Mirrored005]
  InvalidShape = false
  Origin = -> Origin014
  Placement = pos=(0,130,0) rot=(0,0,1;0rad)
  SingleSolid = true
  Tip = -> Mirrored005
  TreeRank = 246
  ValidateShape = true
  _ExportChildren = -> [Pad011,Pocket014,Import003,Pocket017,Pad013,Chamfer027,Fillet010,Pocket028,Mirrored005]
  _GroupVersion = 1
FEATURE [PartDesign::FeatureBase] Clone003
  BaseFeature = -> Pad017
  FixShape = 1
  InvalidShape = false
  NewSolid = false
  Suppress = false
  TreeRank = 518
  ValidateShape = true
FEATURE [PartDesign::Pocket] Pocket029
  AddSubType = 1
  AlongSketchNormal = false
  AutoTaperInnerAngle = true
  BaseFeature = -> Clone003
  CheckUpToFaceLimits = true
  ClaimChildren = false
  Direction = (1,0,0)
  Fit = 0
  FitJoin = 0
  FixShape = 1
  InnerFit = 0
  InnerFitJoin = 0
  InvalidShape = false
  Length = 16
  Length2 = 10
  Linearize = true
  NewSolid = false
  Profile = -> Clone003 [Face25]
  Refine = true
  Suppress = false
  TaperInnerAngle = 0
  TaperInnerAngleRev = 0
  TreeRank = 520
  Type = 0
  ValidateShape = true
  _ProfileBasedVersion = 1
  _Version = 1
FEATURE [Sketcher::SketchObject] Sketch054
  ArcFitTolerance = 1e-06
  AttachmentSupport = -> [Pocket029]
  ExternalBSplineMaxDegree = 5
  ExternalBSplineTolerance = 0.0001
  ExternalGeometry = -> [Pocket029]
  FixShape = 1
  FullyConstrained = true
  InternalTolerance = 1e-06
  InvalidShape = false
  MakeInternals = false
  MapMode = 5
  Placement = pos=(166,0,0) rot=(0.57735,-0.57735,-0.57735;2.0944rad)
  Support = -> [Pocket029]
  TreeRank = 521
  ValidateShape = false
  sketch-geometry (12):
    g0: ArcOfCircle CenterX=40 CenterY=205 CenterZ=0 NormalX=0 NormalY=0 NormalZ=1 AngleXU=0 Radius=5 StartAngle=3.14159 EndAngle=4.71239
    g1: ArcOfCircle CenterX=40 CenterY=175 CenterZ=0 NormalX=0 NormalY=0 NormalZ=1 AngleXU=0 Radius=5 StartAngle=1.5708 EndAngle=3.14159
    g2: LineSegment StartX=40 StartY=210 StartZ=0 EndX=35 EndY=210 EndZ=0
    g3: LineSegment StartX=35 StartY=210 StartZ=0 EndX=35 EndY=205 EndZ=0
    g4: LineSegment StartX=45 StartY=205 StartZ=0 EndX=45 EndY=200 EndZ=0
    g5: LineSegment StartX=40 StartY=200 StartZ=0 EndX=45 EndY=200 EndZ=0
    g6: LineSegment StartX=40 StartY=180 StartZ=0 EndX=45 EndY=180 EndZ=0
    g7: LineSegment StartX=45 StartY=180 StartZ=0 EndX=45 EndY=175 EndZ=0
    g8: LineSegment StartX=40 StartY=170 StartZ=0 EndX=35 EndY=170 EndZ=0
    g9: LineSegment StartX=35 StartY=170 StartZ=0 EndX=35 EndY=175 EndZ=0
    g10: Circle CenterX=40 CenterY=205 CenterZ=0 NormalX=0 NormalY=0 NormalZ=1 AngleXU=0 Radius=2.1
    g11: Circle CenterX=40 CenterY=175 CenterZ=0 NormalX=0 NormalY=0 NormalZ=1 AngleXU=0 Radius=2.1
  constraints (27):
    c: Coincident(g0,g-3)
    c: Equal(g0,g-3)
    c: Coincident(g1,g-4)
    c: Equal(g1,g0)
    c: Coincident(g2,g-3)
    c: Horizontal(g2)
    c: Coincident(g3,g2)
    c: Vertical(g3)
    c: Coincident(g4,g-3)
    c: Vertical(g4)
    c: Horizontal(g5)
    c: Coincident(g5,g4)
    c: Tangent(g1,g6) = 1.5708
    c: Coincident(g6,g7)
    c: Coincident(g7,g-4)
    c: Tangent(g-4,g8) = 1.5708
    c: Coincident(g8,g9)
    c: Vertical(g9)
    c: Tangent(g5,g0) = -1.5708
    c: Tangent(g3,g0) = -1.5708
    c: Tangent(g9,g1) = 1.5708
    c: Horizontal(g6)
    c: Vertical(g7)
    c: Coincident(g10,g0)
    c: Coincident(g11,g1)
    c: Equal(g10,g11)
    c: Diameter(g10) = 4.2
FEATURE [PartDesign::Pad] Pad025
  AddSubType = 0
  AlongSketchNormal = false
  AutoTaperInnerAngle = true
  BaseFeature = -> Pocket029
  CheckUpToFaceLimits = true
  ClaimChildren = false
  Direction = (-1,0,0)
  Fit = 0
  FitJoin = 0
  FixShape = 1
  InnerFit = 0
  InnerFitJoin = 0
  InvalidShape = false
  Length = 8
  Length2 = 10
  Linearize = true
  NewSolid = false
  Profile = -> Sketch054
  ReferenceAxis = -> Sketch054 [N_Axis]
  Refine = true
  Reversed = true
  Suppress = false
  TaperInnerAngle = 0
  TaperInnerAngleRev = 0
  TreeRank = 522
  Type = 0
  ValidateShape = true
  _ProfileBasedVersion = 1
FEATURE [PartDesign::Mirrored] Mirrored006
  AddSubType = 0
  BaseFeature = -> Pad025
  CopyShape = false
  FixShape = 1
  InvalidShape = false
  MirrorPlane = -> Sketch054 [V_Axis]
  NewSolid = false
  OriginalSubs = -> [Pad025]
  Originals = -> [Pad025]
  ParallelTransform = true
  Refine = true
  SubTransform = true
  Suppress = false
  TreeRank = 523
  ValidateShape = true
  _Version = 3
FEATURE [PartDesign::Fillet] Fillet023
  AddSubType = 0
  Base = -> Mirrored006 [Edge82,Edge80,Edge105,Edge88,Edge90,Edge96,Edge98,Edge103]
  BaseFeature = -> Mirrored006
  FixShape = 1
  InvalidShape = false
  NewSolid = false
  Radius = 2
  Refine = true
  SupportTransform = false
  Suppress = false
  TreeRank = 524
  UseAllEdges = false
  ValidateShape = true
FEATURE [PartDesign::Chamfer] Chamfer036
  AddSubType = 0
  Angle = 45
  Base = -> Fillet023 [Edge70,Edge67,Face2,Edge65,Edge57,Edge148,Edge150]
  BaseFeature = -> Fillet023
  ChamferType = 0
  FixShape = 1
  FlipDirection = false
  InvalidShape = false
  NewSolid = false
  Refine = true
  Size = 1
  Size2 = 1
  SupportTransform = false
  Suppress = false
  TreeRank = 525
  UseAllEdges = false
  ValidateShape = true
FEATURE [PartDesign::Chamfer] Chamfer037
  AddSubType = 0
  Angle = 45
  Base = -> Chamfer036 [Edge124,Edge125,Edge128,Edge129,Edge126,Edge127]
  BaseFeature = -> Chamfer036
  ChamferType = 0
  FixShape = 1
  FlipDirection = false
  InvalidShape = false
  NewSolid = false
  Refine = true
  Size = 3
  Size2 = 1
  SupportTransform = false
  Suppress = false
  TreeRank = 526
  UseAllEdges = false
  ValidateShape = true
FEATURE [PartDesign::Body] Body019  label="ContourInsert"
  AutoGroupSolids = false
  BaseFeature = -> Pad017
  ClaimAllChildren = false
  ExportMode = 0
  FixShape = 1
  Group = -> [Clone003,Pocket029,Sketch054,Pad025,Mirrored006,Fillet023,Chamfer036,Chamfer037]
  InvalidShape = false
  Origin = -> Origin023
  Placement = pos=(0,0,-100) rot=(0,0,1;0rad)
  SingleSolid = true
  Tip = -> Chamfer037
  TreeRank = 519
  ValidateShape = false
  _ExportChildren = -> [Clone003,Pocket029,Pad025,Mirrored006,Fillet023,Chamfer036,Chamfer037]
  _GroupVersion = 1
FEATURE [PartDesign::SubShapeBinder] Binder001  label="Binder001(Chamfer037)"
  BindCopyOnChange = 0
  BindMode = 0
  ClaimChildren = false
  Context = -> Part001 [Group007.Part003.Body020.Binder001.]
  EdgeTolerance = 1e-06
  FillStyle = 0
  FixShape = 1
  Fuse = false
  InvalidShape = false
  MakeFace = true
  MergeEdges = true
  OffsetFill = false
  OffsetIntersection = false
  OffsetJoinType = 0
  OffsetOpenResult = false
  Outline = false
  PartialLoad = false
  Relative = true
  SplitEdges = false
  Support = -> [Body019[Chamfer037.Face51]]
  TightBound = false
  TreeRank = 540
  ValidateShape = false
  _Version = 8
FEATURE [Sketcher::SketchObject] Sketch055
  ArcFitTolerance = 1e-06
  AttachmentSupport = -> [Binder001]
  ExternalBSplineMaxDegree = 5
  ExternalBSplineTolerance = 0.0001
  ExternalGeometry = -> [Binder001]
  FixShape = 1
  FullyConstrained = true
  InternalTolerance = 1e-06
  InvalidShape = false
  MakeInternals = false
  MapMode = 5
  Placement = pos=(174,0,0) rot=(0.57735,0.57735,0.57735;2.0944rad)
  Support = -> [Binder001]
  TreeRank = 541
  ValidateShape = false
  sketch-geometry (14):
    g0: ArcOfCircle CenterX=-40 CenterY=105 CenterZ=0 NormalX=0 NormalY=0 NormalZ=1 AngleXU=0 Radius=5 StartAngle=1.5708 EndAngle=3.14159
    g1: LineSegment StartX=-40 StartY=110 StartZ=0 EndX=40 EndY=110 EndZ=0
    g2: ArcOfCircle CenterX=40 CenterY=105 CenterZ=0 NormalX=0 NormalY=0 NormalZ=1 AngleXU=0 Radius=5 StartAngle=2e-16 EndAngle=1.5708
    g3: LineSegment StartX=45 StartY=105 StartZ=0 EndX=45 EndY=75 EndZ=0
    g4: ArcOfCircle CenterX=40 CenterY=75 CenterZ=0 NormalX=0 NormalY=0 NormalZ=1 AngleXU=0 Radius=5 StartAngle=4.71239 EndAngle=6.28319
    g5: LineSegment StartX=40 StartY=70 StartZ=0 EndX=-40 EndY=70 EndZ=0
    g6: ArcOfCircle CenterX=-40 CenterY=75 CenterZ=0 NormalX=0 NormalY=0 NormalZ=1 AngleXU=0 Radius=5 StartAngle=3.14159 EndAngle=4.71239
    g7: LineSegment StartX=-45 StartY=75 StartZ=0 EndX=-45 EndY=105 EndZ=0
    g8: GeomPoint [constr] X=-45 Y=110 Z=0
    g9: GeomPoint [constr] X=45 Y=70 Z=0
    g10: Circle CenterX=-40 CenterY=105 CenterZ=0 NormalX=0 NormalY=0 NormalZ=1 AngleXU=0 Radius=1.6
    g11: Circle CenterX=-40 CenterY=75 CenterZ=0 NormalX=0 NormalY=0 NormalZ=1 AngleXU=0 Radius=1.6
    g12: Circle CenterX=40 CenterY=75 CenterZ=0 NormalX=0 NormalY=0 NormalZ=1 AngleXU=0 Radius=1.6
    g13: Circle CenterX=40 CenterY=105 CenterZ=0 NormalX=0 NormalY=0 NormalZ=1 AngleXU=0 Radius=1.6
  constraints (30):
    c: Tangent(g0,g1) = 1.5708
    c: Tangent(g1,g2) = 1.5708
    c: Tangent(g2,g3) = 1.5708
    c: Tangent(g3,g4) = 1.5708
    c: Tangent(g4,g5) = 1.5708
    c: Tangent(g5,g6) = 1.5708
    c: Tangent(g6,g7) = 1.5708
    c: Tangent(g7,g0) = 1.5708
    c: Horizontal(g1)
    c: Horizontal(g5)
    c: Vertical(g3)
    c: Vertical(g7)
    c: Equal(g2,g4)
    c: Equal(g4,g6)
    c: PointOnObject(g8,g1)
    c: PointOnObject(g8,g7)
    c: PointOnObject(g9,g3)
    c: PointOnObject(g9,g5)
    c: Equal(g0,g-3)
    c: Symmetric(g0,g2,g-2)
    c: DistanceY(g6,g0) = 30
    c: Coincident(g10,g0)
    c: Coincident(g11,g6)
    c: Coincident(g12,g4)
    c: Coincident(g13,g2)
    c: Equal(g13,g12)
    c: Equal(g13,g11)
    c: Equal(g13,g10)
    c: Diameter(g13) = 3.2
    c: Coincident(g0,g-3)
FEATURE [PartDesign::Pad] Pad026
  AddSubType = 0
  AlongSketchNormal = false
  AutoTaperInnerAngle = true
  CheckUpToFaceLimits = true
  ClaimChildren = false
  Direction = (1,0,0)
  Fit = 0
  FitJoin = 0
  FixShape = 1
  InnerFit = 0
  InnerFitJoin = 0
  InvalidShape = false
  Length = 3
  Length2 = 10
  Linearize = true
  NewSolid = false
  Profile = -> Sketch055
  ReferenceAxis = -> Sketch055 [N_Axis]
  Refine = true
  Suppress = false
  TaperInnerAngle = 0
  TaperInnerAngleRev = 0
  TreeRank = 542
  Type = 0
  ValidateShape = true
  _ProfileBasedVersion = 1
FEATURE [PartDesign::Body] Body020  label="PlaqueInsert"
  AutoGroupSolids = false
  ClaimAllChildren = false
  ExportMode = 0
  FixShape = 1
  Group = -> [Binder001,Sketch055,Pad026]
  InvalidShape = false
  Origin = -> Origin025
  SingleSolid = true
  Tip = -> Pad026
  TreeRank = 539
  ValidateShape = false
  _ExportChildren = -> [Binder001,Pad026]
  _GroupVersion = 1
FEATURE [Part::FeaturePython] Screw004  label="M3x12-Vis"  # Fasteners workbench fastener (typed FeaturePython)
  FixShape = 1
  InvalidShape = false
  Placement = pos=(177,-40,75) rot=(0,1,0;1.5708rad)
  TreeRank = 547
  ValidateShape = false
  baseObject = -> Body020 [Edge30]
  diameter = 1
  invert = false
  leftHanded = false
  length = 3
  lengthCustom = 12
  matchOuter = false
  offset = 0
  thread = false
  type = 54
FEATURE [Part::FeaturePython] Screw005  label="M3x12-Vis008"  # Fasteners workbench fastener (typed FeaturePython)
  FixShape = 1
  InvalidShape = false
  Placement = pos=(177,-40,105) rot=(0,1,0;1.5708rad)
  TreeRank = 548
  ValidateShape = false
  baseObject = -> Body020 [Edge27]
  diameter = 1
  invert = false
  leftHanded = false
  length = 3
  lengthCustom = 12
  matchOuter = false
  offset = 0
  thread = false
  type = 54
FEATURE [Part::FeaturePython] Screw006  label="M3x12-Vis007"  # Fasteners workbench fastener (typed FeaturePython)
  FixShape = 1
  InvalidShape = false
  Placement = pos=(177,40,105) rot=(0,1,0;1.5708rad)
  TreeRank = 549
  ValidateShape = false
  baseObject = -> Body020 [Edge36]
  diameter = 1
  invert = false
  leftHanded = false
  length = 3
  lengthCustom = 12
  matchOuter = false
  offset = 0
  thread = false
  type = 54
FEATURE [Part::FeaturePython] Screw007  label="M3x12-Vis009"  # Fasteners workbench fastener (typed FeaturePython)
  FixShape = 1
  InvalidShape = false
  Placement = pos=(177,40,75) rot=(0,1,0;1.5708rad)
  TreeRank = 550
  ValidateShape = false
  baseObject = -> Body020 [Edge33]
  diameter = 1
  invert = false
  leftHanded = false
  length = 3
  lengthCustom = 12
  matchOuter = false
  offset = 0
  thread = false
  type = 54
FEATURE [App::Part] Part003  label="InsertRight"
  ClaimAllChildren = false
  ExportMode = 1
  Group = -> [Body019,Body020,Screw004,Screw006,Screw005,Screw007]
  Origin = -> Origin024
  TreeRank = 529
  _ExportChildren = -> [Body019,Body020,Screw004,Screw006,Screw005,Screw007]
  _GroupVersion = 1
FEATURE [App::Link] Link016  label="InsertLeft"
  AutoLinkLabel = true
  AutoPlacement = true
  LinkPlacement = pos=(0,0,0) rot=(0,0,1;3.14159rad)
  LinkedObject = -> Part003
  Placement = pos=(0,0,0) rot=(0,0,1;3.14159rad)
  SyncGroupVisibility = false
  TreeRank = 551
  _LinkVersion = 1
FEATURE [App::Link] Link017  label="InsertRearRight"
  AutoLinkLabel = true
  AutoPlacement = true
  LinkPlacement = pos=(71,-45,0) rot=(0,0,1;1.5708rad)
  LinkedObject = -> Part003
  Placement = pos=(71,-45,0) rot=(0,0,1;1.5708rad)
  SyncGroupVisibility = false
  TreeRank = 553
  _LinkVersion = 1
FEATURE [App::Link] Link018  label="InsertRearLeft"
  AutoLinkLabel = true
  AutoPlacement = true
  LinkPlacement = pos=(-71,-45,0) rot=(0,0,1;1.5708rad)
  LinkedObject = -> Link017
  Placement = pos=(-71,-45,0) rot=(0,0,1;1.5708rad)
  SyncGroupVisibility = false
  TreeRank = 554
  _LinkVersion = 1
FEATURE [App::DocumentObjectGroup] Group007  label="SideInserts"
  ClaimAllChildren = true
  ExportMode = 1
  Group = -> [Part003,Link016,Link017,Link018]
  TreeRank = 552
  _GroupVersion = 1
FEATURE [TechDraw::DrawProjGroupItem] ProjItem001  label="Front002"
  CoarseView = false
  Direction = (-1,0,0)
  Focus = 100
  HardHidden = false
  IsoCount = 0
  IsoHidden = false
  IsoVisible = false
  LockPosition = true
  Perspective = false
  Rotation = 0
  RotationVector = (0,0,-1)
  ScaleType = 2
  ScrubCount = 0
  SeamHidden = false
  SeamVisible = true
  SmoothHidden = false
  SmoothVisible = true
  Source = -> [Clone]
  TreeRank = 555
  Type = 0
  X = 0
  XDirection = (0,0,-1)
  Y = 0
FEATURE [TechDraw::DrawProjGroup] ProjGroup001
  Anchor = -> ProjItem001
  AutoDistribute = true
  LockPosition = false
  ProjectionType = 0
  Rotation = 0
  ScaleType = 0
  Source = -> [Clone]
  TreeRank = 556
  Views = -> [ProjItem001]
  X = 126.001
  Y = 150.648
  spacingX = 15
  spacingY = 15
FEATURE [TechDraw::DrawPage] Page  label="Laser10mm-Side"
  KeepUpdated = true
  NextBalloonIndex = 1
  ProjectionType = 0
  Template = -> Template
  TreeRank = 291
  Views = -> [ProjGroup001]
FEATURE [TechDraw::DrawProjGroupItem] ProjItem  label="Front009"
  CoarseView = false
  Direction = (0,-1,0)
  Focus = 100
  HardHidden = false
  IsoCount = 0
  IsoHidden = false
  IsoVisible = false
  LockPosition = true
  Perspective = false
  Rotation = 0
  RotationVector = (1,0,0)
  ScaleType = 2
  ScrubCount = 0
  SeamHidden = false
  SeamVisible = false
  SmoothHidden = false
  SmoothVisible = false
  Source = -> [Fillet015]
  TreeRank = 558
  Type = 0
  X = 0
  XDirection = (1,0,0)
  Y = 0
FEATURE [TechDraw::DrawProjGroup] ProjGroup
  Anchor = -> ProjItem
  AutoDistribute = true
  LockPosition = false
  ProjectionType = 0
  Rotation = 0
  ScaleType = 0
  Source = -> [Fillet015]
  TreeRank = 559
  Views = -> [ProjItem]
  X = 210
  Y = 148.5
  spacingX = 15
  spacingY = 15
FEATURE [TechDraw::DrawPage] Page002  label="Laser10mmFront"
  KeepUpdated = true
  NextBalloonIndex = 1
  ProjectionType = 0
  Template = -> Template002
  TreeRank = 306
  Views = -> [ProjGroup]
FEATURE [TechDraw::DrawProjGroupItem] ProjItem008  label="Front010"
  CoarseView = false
  Direction = (0,1,0)
  Focus = 100
  HardHidden = false
  IsoCount = 0
  IsoHidden = false
  IsoVisible = false
  LockPosition = true
  Perspective = false
  Rotation = 0
  RotationVector = (-1,0,0)
  ScaleType = 2
  ScrubCount = 0
  SeamHidden = false
  SeamVisible = false
  SmoothHidden = false
  SmoothVisible = false
  Source = -> [Mirrored005]
  TreeRank = 561
  Type = 0
  X = 0
  XDirection = (-1,0,0)
  Y = 0
FEATURE [TechDraw::DrawProjGroup] ProjGroup008
  Anchor = -> ProjItem008
  AutoDistribute = true
  LockPosition = false
  ProjectionType = 0
  Rotation = 0
  ScaleType = 0
  Source = -> [Mirrored005]
  TreeRank = 562
  Views = -> [ProjItem008]
  X = 180.05
  Y = 178.806
  spacingX = 15
  spacingY = 15
FEATURE [TechDraw::DrawPage] Page003  label="Laser10mmRear"
  KeepUpdated = true
  NextBalloonIndex = 1
  ProjectionType = 0
  Template = -> Template003
  TreeRank = 312
  Views = -> [ProjGroup008]
FEATURE [App::DocumentObjectGroup] Group  label="Structure"
  ClaimAllChildren = true
  ExportMode = 1
  Group = -> [Body007,Body008,Body009,Body011,Body012]
  TreeRank = 564
  _GroupVersion = 1
FEATURE [App::DocumentObjectGroup] Group008  label="Planes"
  ClaimAllChildren = true
  ExportMode = 1
  Group = -> [Origin009,DatumPlane,DatumPlane001,DatumPlane002,DatumPlane003,DatumPlane004]
  TreeRank = 565
  _GroupVersion = 1
FEATURE [App::Part] Part001  label="Crate"
  ClaimAllChildren = false
  ExportMode = 1
  Group = -> [DatumPlane,DatumPlane001,DatumPlane002,DatumPlane003,DatumPlane004,Body007,Body008,Body009,Body011,Body012,Link,Link001,Group003,Body013,Screw,Screw001,Screw002,Screw003,Group005,Body015,Link009,Link002,Group006,Body014,Part003,Link016,Group007,Link017,Link018,Part,Group,Group008]
  Origin = -> Origin009
  TreeRank = 563
  _ExportChildren = -> [Group003,Group006,Group007,Group,Group008]
  _GroupVersion = 1
FEATURE [TechDraw::DrawProjGroupItem] ProjItem009  label="Front011"
  CoarseView = false
  Direction = (0,0,1)
  Focus = 100
  HardHidden = false
  IsoCount = 0
  IsoHidden = false
  IsoVisible = false
  LockPosition = true
  Perspective = false
  Rotation = 0
  RotationVector = (0,1,0)
  ScaleType = 2
  ScrubCount = 0
  SeamHidden = false
  SeamVisible = false
  SmoothHidden = false
  SmoothVisible = false
  Source = -> [Mirrored003]
  TreeRank = 567
  Type = 0
  X = 0
  XDirection = (0,1,0)
  Y = 0
FEATURE [TechDraw::DrawProjGroup] ProjGroup009
  Anchor = -> ProjItem009
  AutoDistribute = true
  LockPosition = false
  ProjectionType = 0
  Rotation = 0
  ScaleType = 0
  Source = -> [Mirrored003]
  TreeRank = 568
  Views = -> [ProjItem009]
  X = 125.152
  Y = 43.3619
  spacingX = 15
  spacingY = 15
FEATURE [TechDraw::DrawPage] Page004  label="Laser3mmPorte"
  KeepUpdated = true
  NextBalloonIndex = 1
  ProjectionType = 0
  Template = -> Template004
  TreeRank = 418
  Views = -> [ProjGroup009]
FEATURE [App::DocumentObjectGroup] Group002  label="Laser"
  ClaimAllChildren = true
  ExportMode = 1
  Group = -> [Page,Page001,Page002,Page003,Page004,Page005,Page006]
  TreeRank = 316
  _GroupVersion = 1
